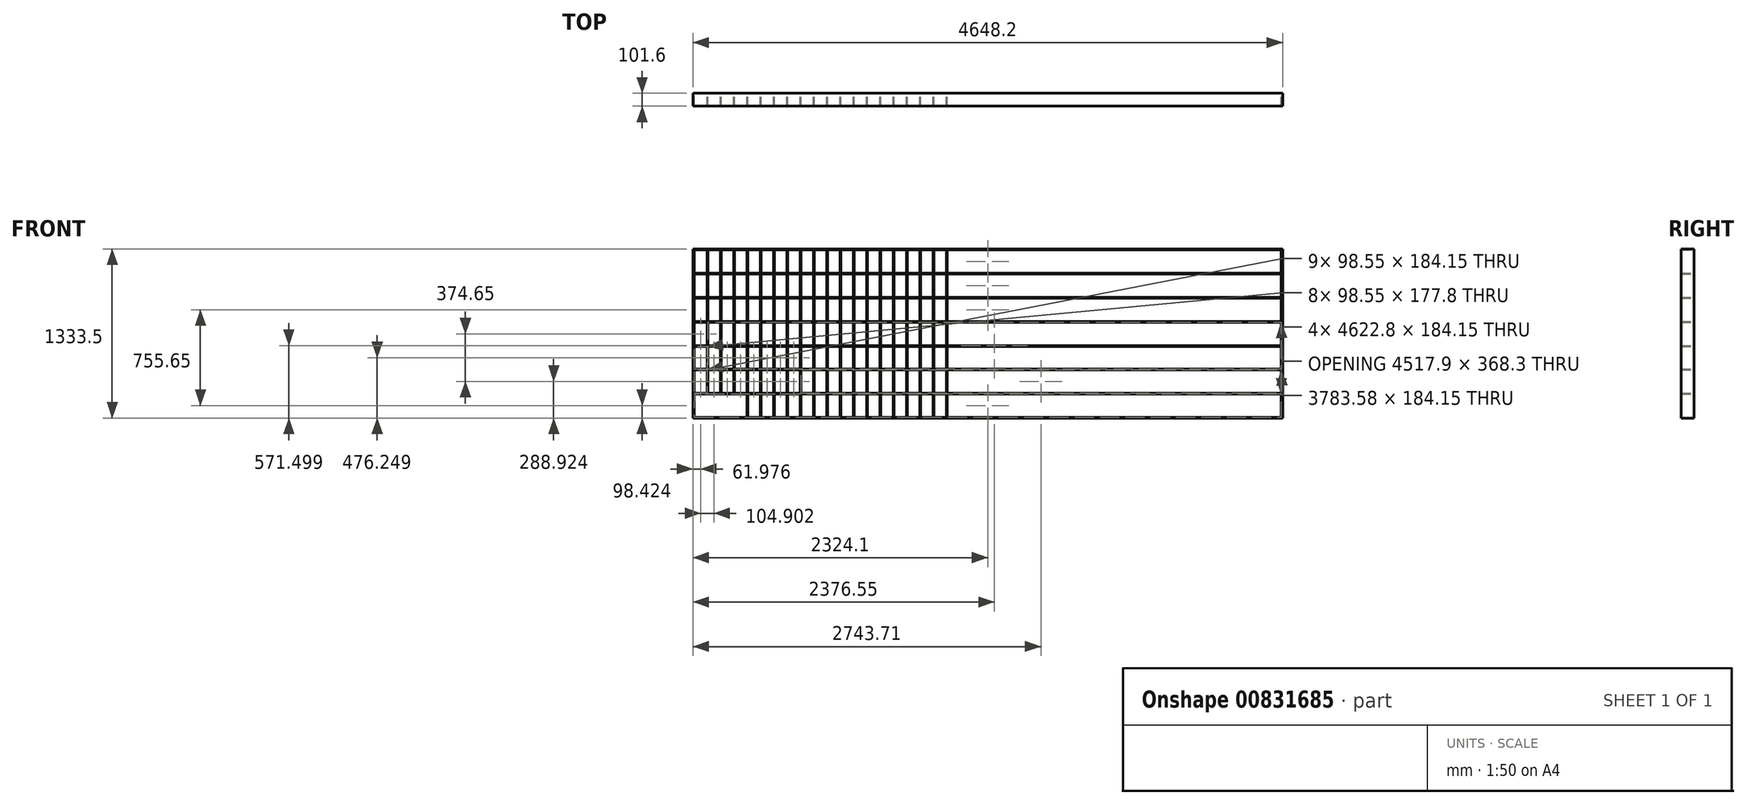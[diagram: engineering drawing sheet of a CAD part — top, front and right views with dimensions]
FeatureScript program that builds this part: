
annotation { "Feature Type Name" : "Feature", "Feature Type Description" : "" }
export const myFeature = defineFeature(function(context is Context, id is Id, definition is map)
    precondition{}
    {
        {
            var Q0;
            Q0=qCreatedBy(makeId("Front.planeOp"),FACE);
            var sketch = newSketch(context, id + "F0", { "sketchPlane" : qUnion([Q0])});
            skLineSegment(sketch, "E0.bottom", {"start": v(-168.1, 48.52) * mm, "end": v(168.1, 48.52) * mm});
            skLineSegment(sketch, "E0.top", {"start": v(-168.1, -48.52) * mm, "end": v(168.1, -48.52) * mm});
            skLineSegment(sketch, "E0.left", {"start": v(-168.1, 48.52) * mm, "end": v(-168.1, -48.52) * mm});
            skLineSegment(sketch, "E0.right", {"start": v(168.1, 48.52) * mm, "end": v(168.1, -48.52) * mm});
            skPoint(sketch, "E0.middle", {"position": v(0, 0) * mm});
            skLineSegment(sketch, "E1.bottom", {"start": v(-2132.34, -583.08) * mm, "end": v(2490.46, -583.08) * mm});
            skLineSegment(sketch, "E1.top", {"start": v(-2132.34, -589.43) * mm, "end": v(2490.46, -589.43) * mm});
            skLineSegment(sketch, "E1.left", {"start": v(-2132.34, -583.08) * mm, "end": v(-2132.34, -589.43) * mm});
            skLineSegment(sketch, "E1.right", {"start": v(2490.46, -583.08) * mm, "end": v(2490.46, -589.43) * mm});
            skLineSegment(sketch, "E2.bottom", {"start": v(-2132.34, -392.58) * mm, "end": v(2490.46, -392.58) * mm});
            skLineSegment(sketch, "E2.top", {"start": v(-2132.34, -398.93) * mm, "end": v(2490.46, -398.93) * mm});
            skLineSegment(sketch, "E2.left", {"start": v(-2132.34, -392.58) * mm, "end": v(-2132.34, -398.93) * mm});
            skLineSegment(sketch, "E2.right", {"start": v(2490.46, -392.58) * mm, "end": v(2490.46, -398.93) * mm});
            skLineSegment(sketch, "E3.bottom", {"start": v(-2132.34, -202.08) * mm, "end": v(2490.46, -202.08) * mm});
            skLineSegment(sketch, "E3.top", {"start": v(-2132.34, -208.43) * mm, "end": v(2490.46, -208.43) * mm});
            skLineSegment(sketch, "E3.left", {"start": v(-2132.34, -202.08) * mm, "end": v(-2132.34, -208.43) * mm});
            skLineSegment(sketch, "E3.right", {"start": v(2490.46, -202.08) * mm, "end": v(2490.46, -208.43) * mm});
            skLineSegment(sketch, "E4.bottom", {"start": v(-2132.34, -17.93) * mm, "end": v(2490.46, -17.93) * mm});
            skLineSegment(sketch, "E4.top", {"start": v(-2132.34, -24.28) * mm, "end": v(2490.46, -24.28) * mm});
            skLineSegment(sketch, "E4.left", {"start": v(-2132.34, -17.93) * mm, "end": v(-2132.34, -24.28) * mm});
            skLineSegment(sketch, "E4.right", {"start": v(2490.46, -17.93) * mm, "end": v(2490.46, -24.28) * mm});
            skLineSegment(sketch, "E5.bottom", {"start": v(-2132.34, 172.57) * mm, "end": v(2490.46, 172.57) * mm});
            skLineSegment(sketch, "E5.top", {"start": v(-2132.34, 166.22) * mm, "end": v(2490.46, 166.22) * mm});
            skLineSegment(sketch, "E5.left", {"start": v(-2132.34, 172.57) * mm, "end": v(-2132.34, 166.22) * mm});
            skLineSegment(sketch, "E5.right", {"start": v(2490.46, 172.57) * mm, "end": v(2490.46, 166.22) * mm});
            skLineSegment(sketch, "E6.bottom", {"start": v(-2132.34, 363.07) * mm, "end": v(2490.46, 363.07) * mm});
            skLineSegment(sketch, "E6.top", {"start": v(-2132.34, 356.72) * mm, "end": v(2490.46, 356.72) * mm});
            skLineSegment(sketch, "E6.left", {"start": v(-2132.34, 363.07) * mm, "end": v(-2132.34, 356.72) * mm});
            skLineSegment(sketch, "E6.right", {"start": v(2490.46, 363.07) * mm, "end": v(2490.46, 356.72) * mm});
            skLineSegment(sketch, "E7.bottom", {"start": v(-2132.34, 553.57) * mm, "end": v(2490.46, 553.57) * mm});
            skLineSegment(sketch, "E7.top", {"start": v(-2132.34, 547.22) * mm, "end": v(2490.46, 547.22) * mm});
            skLineSegment(sketch, "E7.left", {"start": v(-2132.34, 553.57) * mm, "end": v(-2132.34, 547.22) * mm});
            skLineSegment(sketch, "E7.right", {"start": v(2490.46, 553.57) * mm, "end": v(2490.46, 547.22) * mm});
            skLineSegment(sketch, "E8.bottom", {"start": v(-2132.34, 744.07) * mm, "end": v(2490.46, 744.07) * mm});
            skLineSegment(sketch, "E8.top", {"start": v(-2132.34, 737.72) * mm, "end": v(2490.46, 737.72) * mm});
            skLineSegment(sketch, "E8.left", {"start": v(-2132.34, 744.07) * mm, "end": v(-2132.34, 737.72) * mm});
            skLineSegment(sketch, "E8.right", {"start": v(2490.46, 744.07) * mm, "end": v(2490.46, 737.72) * mm});
            skLineSegment(sketch, "E9.bottom", {"start": v(-2132.34, -589.43) * mm, "end": v(-2145.04, -589.43) * mm});
            skLineSegment(sketch, "E9.top", {"start": v(-2132.34, 744.07) * mm, "end": v(-2145.04, 744.07) * mm});
            skLineSegment(sketch, "E9.left", {"start": v(-2132.34, -589.43) * mm, "end": v(-2132.34, 744.07) * mm});
            skLineSegment(sketch, "E9.right", {"start": v(-2145.04, -589.43) * mm, "end": v(-2145.04, 744.07) * mm});
            skLineSegment(sketch, "E10.bottom", {"start": v(2490.46, -589.43) * mm, "end": v(2503.16, -589.43) * mm});
            skLineSegment(sketch, "E10.top", {"start": v(2490.46, 744.07) * mm, "end": v(2503.16, 744.07) * mm});
            skLineSegment(sketch, "E10.left", {"start": v(2490.46, -589.43) * mm, "end": v(2490.46, 744.07) * mm});
            skLineSegment(sketch, "E10.right", {"start": v(2503.16, -589.43) * mm, "end": v(2503.16, 744.07) * mm});
            skLineSegment(sketch, "E11.bottom", {"start": v(-2033.79, -589.43) * mm, "end": v(-2027.44, -589.43) * mm});
            skLineSegment(sketch, "E11.top", {"start": v(-2033.79, 744.07) * mm, "end": v(-2027.44, 744.07) * mm});
            skLineSegment(sketch, "E11.left", {"start": v(-2033.79, -589.43) * mm, "end": v(-2033.79, 744.07) * mm});
            skLineSegment(sketch, "E11.right", {"start": v(-2027.44, -589.43) * mm, "end": v(-2027.44, 744.07) * mm});
            skLineSegment(sketch, "E12.bottom", {"start": v(-1928.89, 744.07) * mm, "end": v(-1922.54, 744.07) * mm});
            skLineSegment(sketch, "E12.top", {"start": v(-1928.89, -589.43) * mm, "end": v(-1922.54, -589.43) * mm});
            skLineSegment(sketch, "E12.left", {"start": v(-1928.89, 744.07) * mm, "end": v(-1928.89, -589.43) * mm});
            skLineSegment(sketch, "E12.right", {"start": v(-1922.54, 744.07) * mm, "end": v(-1922.54, -589.43) * mm});
            skLineSegment(sketch, "E13.bottom", {"start": v(-1823.98, 744.07) * mm, "end": v(-1817.63, 744.07) * mm});
            skLineSegment(sketch, "E13.top", {"start": v(-1823.98, -589.43) * mm, "end": v(-1817.63, -589.43) * mm});
            skLineSegment(sketch, "E13.left", {"start": v(-1823.98, 744.07) * mm, "end": v(-1823.98, -589.43) * mm});
            skLineSegment(sketch, "E13.right", {"start": v(-1817.63, 744.07) * mm, "end": v(-1817.63, -589.43) * mm});
            skLineSegment(sketch, "E14.bottom", {"start": v(-1719.08, 744.07) * mm, "end": v(-1712.73, 744.07) * mm});
            skLineSegment(sketch, "E14.top", {"start": v(-1719.08, -589.43) * mm, "end": v(-1712.73, -589.43) * mm});
            skLineSegment(sketch, "E14.left", {"start": v(-1719.08, 744.07) * mm, "end": v(-1719.08, -589.43) * mm});
            skLineSegment(sketch, "E14.right", {"start": v(-1712.73, 744.07) * mm, "end": v(-1712.73, -589.43) * mm});
            skLineSegment(sketch, "E15.bottom", {"start": v(-1614.18, 744.07) * mm, "end": v(-1607.83, 744.07) * mm});
            skLineSegment(sketch, "E15.top", {"start": v(-1614.18, -589.43) * mm, "end": v(-1607.83, -589.43) * mm});
            skLineSegment(sketch, "E15.left", {"start": v(-1614.18, 744.07) * mm, "end": v(-1614.18, -589.43) * mm});
            skLineSegment(sketch, "E15.right", {"start": v(-1607.83, 744.07) * mm, "end": v(-1607.83, -589.43) * mm});
            skLineSegment(sketch, "E16.bottom", {"start": v(-1509.28, 744.07) * mm, "end": v(-1502.93, 744.07) * mm});
            skLineSegment(sketch, "E16.top", {"start": v(-1509.28, -589.43) * mm, "end": v(-1502.93, -589.43) * mm});
            skLineSegment(sketch, "E16.left", {"start": v(-1509.28, 744.07) * mm, "end": v(-1509.28, -589.43) * mm});
            skLineSegment(sketch, "E16.right", {"start": v(-1502.93, 744.07) * mm, "end": v(-1502.93, -589.43) * mm});
            skLineSegment(sketch, "E17.bottom", {"start": v(-1404.38, 744.07) * mm, "end": v(-1398.03, 744.07) * mm});
            skLineSegment(sketch, "E17.top", {"start": v(-1404.38, -589.43) * mm, "end": v(-1398.03, -589.43) * mm});
            skLineSegment(sketch, "E17.left", {"start": v(-1404.38, 744.07) * mm, "end": v(-1404.38, -589.43) * mm});
            skLineSegment(sketch, "E17.right", {"start": v(-1398.03, 744.07) * mm, "end": v(-1398.03, -589.43) * mm});
            skLineSegment(sketch, "E18.bottom", {"start": v(-1299.47, 744.07) * mm, "end": v(-1293.12, 744.07) * mm});
            skLineSegment(sketch, "E18.top", {"start": v(-1299.47, -589.43) * mm, "end": v(-1293.12, -589.43) * mm});
            skLineSegment(sketch, "E18.left", {"start": v(-1299.47, 744.07) * mm, "end": v(-1299.47, -589.43) * mm});
            skLineSegment(sketch, "E18.right", {"start": v(-1293.12, 744.07) * mm, "end": v(-1293.12, -589.43) * mm});
            skLineSegment(sketch, "E19.bottom", {"start": v(-1194.57, 744.07) * mm, "end": v(-1188.22, 744.07) * mm});
            skLineSegment(sketch, "E19.top", {"start": v(-1194.57, -589.43) * mm, "end": v(-1188.22, -589.43) * mm});
            skLineSegment(sketch, "E19.left", {"start": v(-1194.57, 744.07) * mm, "end": v(-1194.57, -589.43) * mm});
            skLineSegment(sketch, "E19.right", {"start": v(-1188.22, 744.07) * mm, "end": v(-1188.22, -589.43) * mm});
            skLineSegment(sketch, "E20.bottom", {"start": v(-1083.32, 744.07) * mm, "end": v(-1089.67, 744.07) * mm});
            skLineSegment(sketch, "E20.top", {"start": v(-1083.32, -589.43) * mm, "end": v(-1089.67, -589.43) * mm});
            skLineSegment(sketch, "E20.left", {"start": v(-1083.32, 744.07) * mm, "end": v(-1083.32, -589.43) * mm});
            skLineSegment(sketch, "E20.right", {"start": v(-1089.67, 744.07) * mm, "end": v(-1089.67, -589.43) * mm});
            skLineSegment(sketch, "E21.bottom", {"start": v(-984.77, 744.07) * mm, "end": v(-978.42, 744.07) * mm});
            skLineSegment(sketch, "E21.top", {"start": v(-984.77, -589.43) * mm, "end": v(-978.42, -589.43) * mm});
            skLineSegment(sketch, "E21.left", {"start": v(-984.77, 744.07) * mm, "end": v(-984.77, -589.43) * mm});
            skLineSegment(sketch, "E21.right", {"start": v(-978.42, 744.07) * mm, "end": v(-978.42, -589.43) * mm});
            skLineSegment(sketch, "E22.bottom", {"start": v(-879.87, 744.07) * mm, "end": v(-873.52, 744.07) * mm});
            skLineSegment(sketch, "E22.top", {"start": v(-879.87, -589.43) * mm, "end": v(-873.52, -589.43) * mm});
            skLineSegment(sketch, "E22.left", {"start": v(-879.87, 744.07) * mm, "end": v(-879.87, -589.43) * mm});
            skLineSegment(sketch, "E22.right", {"start": v(-873.52, 744.07) * mm, "end": v(-873.52, -589.43) * mm});
            skLineSegment(sketch, "E23.bottom", {"start": v(-774.96, 744.07) * mm, "end": v(-768.61, 744.07) * mm});
            skLineSegment(sketch, "E23.top", {"start": v(-774.96, -589.43) * mm, "end": v(-768.61, -589.43) * mm});
            skLineSegment(sketch, "E23.left", {"start": v(-774.96, 744.07) * mm, "end": v(-774.96, -589.43) * mm});
            skLineSegment(sketch, "E23.right", {"start": v(-768.61, 744.07) * mm, "end": v(-768.61, -589.43) * mm});
            skLineSegment(sketch, "E24.top", {"start": v(-755.75, -589.43) * mm, "end": v(-735.44, -589.43) * mm});
            skLineSegment(sketch, "E25.bottom", {"start": v(-670.06, 744.07) * mm, "end": v(-663.71, 744.07) * mm});
            skLineSegment(sketch, "E25.top", {"start": v(-670.06, -589.43) * mm, "end": v(-663.71, -589.43) * mm});
            skLineSegment(sketch, "E25.left", {"start": v(-670.06, 744.07) * mm, "end": v(-670.06, -589.43) * mm});
            skLineSegment(sketch, "E25.right", {"start": v(-663.71, 744.07) * mm, "end": v(-663.71, -589.43) * mm});
            skLineSegment(sketch, "E26.bottom", {"start": v(-565.16, 744.07) * mm, "end": v(-558.8, 744.07) * mm});
            skLineSegment(sketch, "E26.top", {"start": v(-565.16, -589.43) * mm, "end": v(-558.8, -589.43) * mm});
            skLineSegment(sketch, "E26.left", {"start": v(-565.16, 744.07) * mm, "end": v(-565.16, -589.43) * mm});
            skLineSegment(sketch, "E26.right", {"start": v(-558.8, 744.07) * mm, "end": v(-558.8, -589.43) * mm});
            skLineSegment(sketch, "E27.bottom", {"start": v(-460.26, 744.07) * mm, "end": v(-453.9, 744.07) * mm});
            skLineSegment(sketch, "E27.top", {"start": v(-460.26, -589.43) * mm, "end": v(-453.9, -589.43) * mm});
            skLineSegment(sketch, "E27.left", {"start": v(-460.26, 744.07) * mm, "end": v(-460.26, -589.43) * mm});
            skLineSegment(sketch, "E27.right", {"start": v(-453.9, 744.07) * mm, "end": v(-453.9, -589.43) * mm});
            skLineSegment(sketch, "E28.bottom", {"start": v(-355.36, 744.07) * mm, "end": v(-349, 744.07) * mm});
            skLineSegment(sketch, "E28.top", {"start": v(-355.36, -589.43) * mm, "end": v(-349, -589.43) * mm});
            skLineSegment(sketch, "E28.left", {"start": v(-355.36, 744.07) * mm, "end": v(-355.36, -589.43) * mm});
            skLineSegment(sketch, "E28.right", {"start": v(-349, 744.07) * mm, "end": v(-349, -589.43) * mm});
            skLineSegment(sketch, "E29.bottom", {"start": v(-244.1, 744.07) * mm, "end": v(-250.45, 744.07) * mm});
            skLineSegment(sketch, "E29.top", {"start": v(-244.1, -589.43) * mm, "end": v(-250.45, -589.43) * mm});
            skLineSegment(sketch, "E29.left", {"start": v(-244.1, 744.07) * mm, "end": v(-244.1, -589.43) * mm});
            skLineSegment(sketch, "E29.right", {"start": v(-250.45, 744.07) * mm, "end": v(-250.45, -589.43) * mm});
            skLineSegment(sketch, "E30.bottom", {"start": v(-139.2, 744.07) * mm, "end": v(-145.55, 744.07) * mm});
            skLineSegment(sketch, "E30.top", {"start": v(-139.2, -589.43) * mm, "end": v(-145.55, -589.43) * mm});
            skLineSegment(sketch, "E30.left", {"start": v(-139.2, 744.07) * mm, "end": v(-139.2, -589.43) * mm});
            skLineSegment(sketch, "E30.right", {"start": v(-145.55, 744.07) * mm, "end": v(-145.55, -589.43) * mm});
            skSolve(sketch);
        }
        {
            var Q0;
            {var subQ0=sQuery(id+"F0.wireOp",EDGE,"E1.bottom");Q0=makeQuery(id+"F0.imprint","IMPRINT",FACE,{"disambiguationData":[TD([[makeQuery(id+"F0.imprint","IMPRINT",EDGE,{"derivedFrom":subQ0}),1.0]])]});}
            var sketch = newSketch(context, id + "F1", { "sketchPlane" : qUnion([Q0])});
            skSolve(sketch);
        }
        {
            var Q0;
            Q0 = qSketchRegion(id + "F0", true);
            var Q1;
            {var subQ0=sQuery(id+"F0.wireOp",EDGE,"E7.bottom");Q1=makeQuery(id+"F0.imprint","IMPRINT",FACE,{"disambiguationData":[TD([[makeQuery(id+"F0.imprint","IMPRINT",EDGE,{"derivedFrom":subQ0}),-1.0]])]});}
            var Q2;
            {var subQ0=sQuery(id+"F0.wireOp",EDGE,"E6.bottom");Q2=makeQuery(id+"F0.imprint","IMPRINT",FACE,{"disambiguationData":[TD([[makeQuery(id+"F0.imprint","IMPRINT",EDGE,{"derivedFrom":subQ0}),-1.0]])]});}
            var Q3;
            {var subQ0=sQuery(id+"F0.wireOp",EDGE,"E5.bottom");Q3=makeQuery(id+"F0.imprint","IMPRINT",FACE,{"disambiguationData":[TD([[makeQuery(id+"F0.imprint","IMPRINT",EDGE,{"derivedFrom":subQ0}),-1.0]])]});}
            var Q4;
            {var subQ0=sQuery(id+"F0.wireOp",EDGE,"E4.bottom");var subQ1=sQuery(id+"F0.wireOp",EDGE,"E0.left");var subQ2=makeQuery(id+"F0.imprint","INTERSECT",VERTEX,{"derivedFrom":[subQ1,subQ0]});Q4=makeQuery(id+"F0.imprint","IMPRINT",FACE,{"disambiguationData":[TD([[makeQuery(id+"F0.imprint","IMPRINT",EDGE,{"disambiguationData":[TD([[subQ2,-1.0]])],"derivedFrom":subQ1}),-1.0]])]});}
            var Q5;
            {var subQ0=sQuery(id+"F0.wireOp",EDGE,"E3.bottom");Q5=makeQuery(id+"F0.imprint","IMPRINT",FACE,{"disambiguationData":[TD([[makeQuery(id+"F0.imprint","IMPRINT",EDGE,{"derivedFrom":subQ0}),-1.0]])]});}
            var Q6;
            {var subQ0=sQuery(id+"F0.wireOp",EDGE,"E2.bottom");Q6=makeQuery(id+"F0.imprint","IMPRINT",FACE,{"disambiguationData":[TD([[makeQuery(id+"F0.imprint","IMPRINT",EDGE,{"derivedFrom":subQ0}),-1.0]])]});}
            var Q7;
            {var subQ0=sQuery(id+"F0.wireOp",EDGE,"E4.bottom");var subQ1=sQuery(id+"F0.wireOp",EDGE,"E0.left");var subQ2=makeQuery(id+"F0.imprint","INTERSECT",VERTEX,{"derivedFrom":[subQ1,subQ0]});Q7=makeQuery(id+"F0.imprint","IMPRINT",FACE,{"disambiguationData":[TD([[makeQuery(id+"F0.imprint","IMPRINT",EDGE,{"disambiguationData":[TD([[subQ2,-1.0]])],"derivedFrom":subQ1}),1.0]])]});}
            var Q8;
            {var subQ0=sQuery(id+"F0.wireOp",EDGE,"E4.bottom");var subQ1=sQuery(id+"F0.wireOp",EDGE,"E0.right");var subQ2=makeQuery(id+"F0.imprint","INTERSECT",VERTEX,{"derivedFrom":[subQ1,subQ0]});Q8=makeQuery(id+"F0.imprint","IMPRINT",FACE,{"disambiguationData":[TD([[makeQuery(id+"F0.imprint","IMPRINT",EDGE,{"disambiguationData":[TD([[subQ2,-1.0]])],"derivedFrom":subQ1}),1.0]])]});}
            extrude(context, id + "F2", {"entities" : qUnion([Q0, Q1, Q2, Q3, Q4, Q5, Q6, Q7, Q8]), "depth" : 101.6 * mm, "offsetDistance" : 25.4 * mm});
        }
        {
            var Q0;
            {var subQ0=sQuery(id+"F0.wireOp",EDGE,"E4.bottom");var subQ1=sQuery(id+"F0.wireOp",EDGE,"E0.right");var subQ2=makeQuery(id+"F0.imprint","INTERSECT",VERTEX,{"derivedFrom":[subQ1,subQ0]});Q0=makeQuery(id+"F0.imprint","IMPRINT",FACE,{"disambiguationData":[TD([[makeQuery(id+"F0.imprint","IMPRINT",EDGE,{"disambiguationData":[TD([[subQ2,-1.0]])],"derivedFrom":subQ1}),-1.0]])]});}
            var Q1;
            {var subQ0=sQuery(id+"F0.wireOp",EDGE,"E28.right");var subQ1=sQuery(id+"F0.wireOp",EDGE,"E4.bottom");var subQ2=makeQuery(id+"F0.imprint","INTERSECT",VERTEX,{"derivedFrom":[subQ1,subQ0]});Q1=makeQuery(id+"F0.imprint","IMPRINT",FACE,{"disambiguationData":[TD([[makeQuery(id+"F0.imprint","IMPRINT",EDGE,{"disambiguationData":[TD([[subQ2,-1.0]])],"derivedFrom":subQ1}),-1.0]])]});}
            var Q2;
            {var subQ0=sQuery(id+"F0.wireOp",EDGE,"E27.right");var subQ1=sQuery(id+"F0.wireOp",EDGE,"E4.bottom");var subQ2=makeQuery(id+"F0.imprint","INTERSECT",VERTEX,{"derivedFrom":[subQ1,subQ0]});Q2=makeQuery(id+"F0.imprint","IMPRINT",FACE,{"disambiguationData":[TD([[makeQuery(id+"F0.imprint","IMPRINT",EDGE,{"disambiguationData":[TD([[subQ2,-1.0]])],"derivedFrom":subQ1}),-1.0]])]});}
            var Q3;
            {var subQ0=sQuery(id+"F0.wireOp",EDGE,"E26.right");var subQ1=sQuery(id+"F0.wireOp",EDGE,"E4.bottom");var subQ2=makeQuery(id+"F0.imprint","INTERSECT",VERTEX,{"derivedFrom":[subQ1,subQ0]});Q3=makeQuery(id+"F0.imprint","IMPRINT",FACE,{"disambiguationData":[TD([[makeQuery(id+"F0.imprint","IMPRINT",EDGE,{"disambiguationData":[TD([[subQ2,-1.0]])],"derivedFrom":subQ1}),-1.0]])]});}
            var Q4;
            {var subQ0=sQuery(id+"F0.wireOp",EDGE,"E25.right");var subQ1=sQuery(id+"F0.wireOp",EDGE,"E4.bottom");var subQ2=makeQuery(id+"F0.imprint","INTERSECT",VERTEX,{"derivedFrom":[subQ1,subQ0]});Q4=makeQuery(id+"F0.imprint","IMPRINT",FACE,{"disambiguationData":[TD([[makeQuery(id+"F0.imprint","IMPRINT",EDGE,{"disambiguationData":[TD([[subQ2,-1.0]])],"derivedFrom":subQ1}),-1.0]])]});}
            var Q5;
            {var subQ0=sQuery(id+"F0.wireOp",EDGE,"E23.right");var subQ1=sQuery(id+"F0.wireOp",EDGE,"E4.bottom");var subQ2=makeQuery(id+"F0.imprint","INTERSECT",VERTEX,{"derivedFrom":[subQ1,subQ0]});Q5=makeQuery(id+"F0.imprint","IMPRINT",FACE,{"disambiguationData":[TD([[makeQuery(id+"F0.imprint","IMPRINT",EDGE,{"disambiguationData":[TD([[subQ2,-1.0]])],"derivedFrom":subQ1}),-1.0]])]});}
            var Q6;
            {var subQ0=sQuery(id+"F0.wireOp",EDGE,"E22.right");var subQ1=sQuery(id+"F0.wireOp",EDGE,"E4.bottom");var subQ2=makeQuery(id+"F0.imprint","INTERSECT",VERTEX,{"derivedFrom":[subQ1,subQ0]});Q6=makeQuery(id+"F0.imprint","IMPRINT",FACE,{"disambiguationData":[TD([[makeQuery(id+"F0.imprint","IMPRINT",EDGE,{"disambiguationData":[TD([[subQ2,-1.0]])],"derivedFrom":subQ1}),-1.0]])]});}
            var Q7;
            {var subQ0=sQuery(id+"F0.wireOp",EDGE,"E21.right");var subQ1=sQuery(id+"F0.wireOp",EDGE,"E4.bottom");var subQ2=makeQuery(id+"F0.imprint","INTERSECT",VERTEX,{"derivedFrom":[subQ1,subQ0]});Q7=makeQuery(id+"F0.imprint","IMPRINT",FACE,{"disambiguationData":[TD([[makeQuery(id+"F0.imprint","IMPRINT",EDGE,{"disambiguationData":[TD([[subQ2,-1.0]])],"derivedFrom":subQ1}),-1.0]])]});}
            var Q8;
            {var subQ0=sQuery(id+"F0.wireOp",EDGE,"E19.right");var subQ1=sQuery(id+"F0.wireOp",EDGE,"E4.bottom");var subQ2=makeQuery(id+"F0.imprint","INTERSECT",VERTEX,{"derivedFrom":[subQ1,subQ0]});Q8=makeQuery(id+"F0.imprint","IMPRINT",FACE,{"disambiguationData":[TD([[makeQuery(id+"F0.imprint","IMPRINT",EDGE,{"disambiguationData":[TD([[subQ2,-1.0]])],"derivedFrom":subQ1}),-1.0]])]});}
            var Q9;
            {var subQ0=sQuery(id+"F0.wireOp",EDGE,"E20.left");var subQ1=sQuery(id+"F0.wireOp",EDGE,"E4.bottom");var subQ2=makeQuery(id+"F0.imprint","INTERSECT",VERTEX,{"derivedFrom":[subQ1,subQ0]});Q9=makeQuery(id+"F0.imprint","IMPRINT",FACE,{"disambiguationData":[TD([[makeQuery(id+"F0.imprint","IMPRINT",EDGE,{"disambiguationData":[TD([[subQ2,-1.0]])],"derivedFrom":subQ1}),-1.0]])]});}
            var Q10;
            {var subQ0=sQuery(id+"F0.wireOp",EDGE,"E9.left");var subQ1=sQuery(id+"F0.wireOp",EDGE,"E4.bottom");var subQ2=makeQuery(id+"F0.imprint","INTERSECT",VERTEX,{"derivedFrom":[subQ1,subQ0]});Q10=makeQuery(id+"F0.imprint","IMPRINT",FACE,{"disambiguationData":[TD([[makeQuery(id+"F0.imprint","IMPRINT",EDGE,{"disambiguationData":[TD([[subQ2,-1.0]])],"derivedFrom":subQ1}),-1.0]])]});}
            var Q11;
            {var subQ0=sQuery(id+"F0.wireOp",EDGE,"E11.left");var subQ1=sQuery(id+"F0.wireOp",EDGE,"E1.bottom");var subQ2=makeQuery(id+"F0.imprint","INTERSECT",VERTEX,{"derivedFrom":[subQ1,subQ0]});Q11=makeQuery(id+"F1.imprint","IMPRINT",FACE,{"disambiguationData":[TD([[makeQuery(id+"F1.imprint","IMPRINT",EDGE,{"derivedFrom":makeQuery(id+"F0.imprint","IMPRINT",EDGE,{"disambiguationData":[TD([[subQ2,-1.0]])],"derivedFrom":subQ1})}),1.0]])]});}
            var Q12;
            {var subQ0=sQuery(id+"F0.wireOp",EDGE,"E11.left");var subQ1=sQuery(id+"F0.wireOp",EDGE,"E2.bottom");var subQ2=makeQuery(id+"F0.imprint","INTERSECT",VERTEX,{"derivedFrom":[subQ1,subQ0]});Q12=makeQuery(id+"F0.imprint","IMPRINT",FACE,{"disambiguationData":[TD([[makeQuery(id+"F0.imprint","IMPRINT",EDGE,{"disambiguationData":[TD([[subQ2,-1.0]])],"derivedFrom":subQ1}),1.0]])]});}
            var Q13;
            {var subQ0=sQuery(id+"F0.wireOp",EDGE,"E11.left");var subQ1=sQuery(id+"F0.wireOp",EDGE,"E3.bottom");var subQ2=makeQuery(id+"F0.imprint","INTERSECT",VERTEX,{"derivedFrom":[subQ1,subQ0]});Q13=makeQuery(id+"F0.imprint","IMPRINT",FACE,{"disambiguationData":[TD([[makeQuery(id+"F0.imprint","IMPRINT",EDGE,{"disambiguationData":[TD([[subQ2,-1.0]])],"derivedFrom":subQ1}),1.0]])]});}
            var Q14;
            {var subQ0=sQuery(id+"F0.wireOp",EDGE,"E11.right");var subQ1=sQuery(id+"F0.wireOp",EDGE,"E4.bottom");var subQ2=makeQuery(id+"F0.imprint","INTERSECT",VERTEX,{"derivedFrom":[subQ1,subQ0]});Q14=makeQuery(id+"F0.imprint","IMPRINT",FACE,{"disambiguationData":[TD([[makeQuery(id+"F0.imprint","IMPRINT",EDGE,{"disambiguationData":[TD([[subQ2,-1.0]])],"derivedFrom":subQ1}),-1.0]])]});}
            var Q15;
            {var subQ0=sQuery(id+"F0.wireOp",EDGE,"E18.right");var subQ1=sQuery(id+"F0.wireOp",EDGE,"E4.bottom");var subQ2=makeQuery(id+"F0.imprint","INTERSECT",VERTEX,{"derivedFrom":[subQ1,subQ0]});Q15=makeQuery(id+"F0.imprint","IMPRINT",FACE,{"disambiguationData":[TD([[makeQuery(id+"F0.imprint","IMPRINT",EDGE,{"disambiguationData":[TD([[subQ2,-1.0]])],"derivedFrom":subQ1}),-1.0]])]});}
            var Q16;
            {var subQ0=sQuery(id+"F0.wireOp",EDGE,"E17.right");var subQ1=sQuery(id+"F0.wireOp",EDGE,"E4.bottom");var subQ2=makeQuery(id+"F0.imprint","INTERSECT",VERTEX,{"derivedFrom":[subQ1,subQ0]});Q16=makeQuery(id+"F0.imprint","IMPRINT",FACE,{"disambiguationData":[TD([[makeQuery(id+"F0.imprint","IMPRINT",EDGE,{"disambiguationData":[TD([[subQ2,-1.0]])],"derivedFrom":subQ1}),-1.0]])]});}
            var Q17;
            {var subQ0=sQuery(id+"F0.wireOp",EDGE,"E16.right");var subQ1=sQuery(id+"F0.wireOp",EDGE,"E4.bottom");var subQ2=makeQuery(id+"F0.imprint","INTERSECT",VERTEX,{"derivedFrom":[subQ1,subQ0]});Q17=makeQuery(id+"F0.imprint","IMPRINT",FACE,{"disambiguationData":[TD([[makeQuery(id+"F0.imprint","IMPRINT",EDGE,{"disambiguationData":[TD([[subQ2,-1.0]])],"derivedFrom":subQ1}),-1.0]])]});}
            var Q18;
            {var subQ0=sQuery(id+"F0.wireOp",EDGE,"E15.right");var subQ1=sQuery(id+"F0.wireOp",EDGE,"E4.bottom");var subQ2=makeQuery(id+"F0.imprint","INTERSECT",VERTEX,{"derivedFrom":[subQ1,subQ0]});Q18=makeQuery(id+"F0.imprint","IMPRINT",FACE,{"disambiguationData":[TD([[makeQuery(id+"F0.imprint","IMPRINT",EDGE,{"disambiguationData":[TD([[subQ2,-1.0]])],"derivedFrom":subQ1}),-1.0]])]});}
            var Q19;
            {var subQ0=sQuery(id+"F0.wireOp",EDGE,"E14.right");var subQ1=sQuery(id+"F0.wireOp",EDGE,"E4.bottom");var subQ2=makeQuery(id+"F0.imprint","INTERSECT",VERTEX,{"derivedFrom":[subQ1,subQ0]});Q19=makeQuery(id+"F0.imprint","IMPRINT",FACE,{"disambiguationData":[TD([[makeQuery(id+"F0.imprint","IMPRINT",EDGE,{"disambiguationData":[TD([[subQ2,-1.0]])],"derivedFrom":subQ1}),-1.0]])]});}
            var Q20;
            {var subQ0=sQuery(id+"F0.wireOp",EDGE,"E13.right");var subQ1=sQuery(id+"F0.wireOp",EDGE,"E4.bottom");var subQ2=makeQuery(id+"F0.imprint","INTERSECT",VERTEX,{"derivedFrom":[subQ1,subQ0]});Q20=makeQuery(id+"F0.imprint","IMPRINT",FACE,{"disambiguationData":[TD([[makeQuery(id+"F0.imprint","IMPRINT",EDGE,{"disambiguationData":[TD([[subQ2,-1.0]])],"derivedFrom":subQ1}),-1.0]])]});}
            var Q21;
            {var subQ0=sQuery(id+"F0.wireOp",EDGE,"E18.left");var subQ1=sQuery(id+"F0.wireOp",EDGE,"E3.bottom");var subQ2=makeQuery(id+"F0.imprint","INTERSECT",VERTEX,{"derivedFrom":[subQ1,subQ0]});Q21=makeQuery(id+"F0.imprint","IMPRINT",FACE,{"disambiguationData":[TD([[makeQuery(id+"F0.imprint","IMPRINT",EDGE,{"disambiguationData":[TD([[subQ2,-1.0]])],"derivedFrom":subQ1}),1.0]])]});}
            var Q22;
            {var subQ0=sQuery(id+"F0.wireOp",EDGE,"E17.left");var subQ1=sQuery(id+"F0.wireOp",EDGE,"E3.bottom");var subQ2=makeQuery(id+"F0.imprint","INTERSECT",VERTEX,{"derivedFrom":[subQ1,subQ0]});Q22=makeQuery(id+"F0.imprint","IMPRINT",FACE,{"disambiguationData":[TD([[makeQuery(id+"F0.imprint","IMPRINT",EDGE,{"disambiguationData":[TD([[subQ2,-1.0]])],"derivedFrom":subQ1}),1.0]])]});}
            var Q23;
            {var subQ0=sQuery(id+"F0.wireOp",EDGE,"E16.left");var subQ1=sQuery(id+"F0.wireOp",EDGE,"E3.bottom");var subQ2=makeQuery(id+"F0.imprint","INTERSECT",VERTEX,{"derivedFrom":[subQ1,subQ0]});Q23=makeQuery(id+"F0.imprint","IMPRINT",FACE,{"disambiguationData":[TD([[makeQuery(id+"F0.imprint","IMPRINT",EDGE,{"disambiguationData":[TD([[subQ2,-1.0]])],"derivedFrom":subQ1}),1.0]])]});}
            var Q24;
            {var subQ0=sQuery(id+"F0.wireOp",EDGE,"E12.right");var subQ1=sQuery(id+"F0.wireOp",EDGE,"E4.bottom");var subQ2=makeQuery(id+"F0.imprint","INTERSECT",VERTEX,{"derivedFrom":[subQ1,subQ0]});Q24=makeQuery(id+"F0.imprint","IMPRINT",FACE,{"disambiguationData":[TD([[makeQuery(id+"F0.imprint","IMPRINT",EDGE,{"disambiguationData":[TD([[subQ2,-1.0]])],"derivedFrom":subQ1}),-1.0]])]});}
            var Q25;
            {var subQ0=sQuery(id+"F0.wireOp",EDGE,"E12.left");var subQ1=sQuery(id+"F0.wireOp",EDGE,"E3.bottom");var subQ2=makeQuery(id+"F0.imprint","INTERSECT",VERTEX,{"derivedFrom":[subQ1,subQ0]});Q25=makeQuery(id+"F0.imprint","IMPRINT",FACE,{"disambiguationData":[TD([[makeQuery(id+"F0.imprint","IMPRINT",EDGE,{"disambiguationData":[TD([[subQ2,-1.0]])],"derivedFrom":subQ1}),1.0]])]});}
            var Q26;
            {var subQ0=sQuery(id+"F0.wireOp",EDGE,"E13.left");var subQ1=sQuery(id+"F0.wireOp",EDGE,"E3.bottom");var subQ2=makeQuery(id+"F0.imprint","INTERSECT",VERTEX,{"derivedFrom":[subQ1,subQ0]});Q26=makeQuery(id+"F0.imprint","IMPRINT",FACE,{"disambiguationData":[TD([[makeQuery(id+"F0.imprint","IMPRINT",EDGE,{"disambiguationData":[TD([[subQ2,-1.0]])],"derivedFrom":subQ1}),1.0]])]});}
            var Q27;
            {var subQ0=sQuery(id+"F0.wireOp",EDGE,"E14.left");var subQ1=sQuery(id+"F0.wireOp",EDGE,"E3.bottom");var subQ2=makeQuery(id+"F0.imprint","INTERSECT",VERTEX,{"derivedFrom":[subQ1,subQ0]});Q27=makeQuery(id+"F0.imprint","IMPRINT",FACE,{"disambiguationData":[TD([[makeQuery(id+"F0.imprint","IMPRINT",EDGE,{"disambiguationData":[TD([[subQ2,-1.0]])],"derivedFrom":subQ1}),1.0]])]});}
            var Q28;
            {var subQ0=sQuery(id+"F0.wireOp",EDGE,"E15.left");var subQ1=sQuery(id+"F0.wireOp",EDGE,"E3.bottom");var subQ2=makeQuery(id+"F0.imprint","INTERSECT",VERTEX,{"derivedFrom":[subQ1,subQ0]});Q28=makeQuery(id+"F0.imprint","IMPRINT",FACE,{"disambiguationData":[TD([[makeQuery(id+"F0.imprint","IMPRINT",EDGE,{"disambiguationData":[TD([[subQ2,-1.0]])],"derivedFrom":subQ1}),1.0]])]});}
            var Q29;
            {var subQ0=sQuery(id+"F0.wireOp",EDGE,"E15.left");var subQ1=sQuery(id+"F0.wireOp",EDGE,"E2.bottom");var subQ2=makeQuery(id+"F0.imprint","INTERSECT",VERTEX,{"derivedFrom":[subQ1,subQ0]});Q29=makeQuery(id+"F0.imprint","IMPRINT",FACE,{"disambiguationData":[TD([[makeQuery(id+"F0.imprint","IMPRINT",EDGE,{"disambiguationData":[TD([[subQ2,-1.0]])],"derivedFrom":subQ1}),1.0]])]});}
            var Q30;
            {var subQ0=sQuery(id+"F0.wireOp",EDGE,"E16.left");var subQ1=sQuery(id+"F0.wireOp",EDGE,"E2.bottom");var subQ2=makeQuery(id+"F0.imprint","INTERSECT",VERTEX,{"derivedFrom":[subQ1,subQ0]});Q30=makeQuery(id+"F0.imprint","IMPRINT",FACE,{"disambiguationData":[TD([[makeQuery(id+"F0.imprint","IMPRINT",EDGE,{"disambiguationData":[TD([[subQ2,-1.0]])],"derivedFrom":subQ1}),1.0]])]});}
            var Q31;
            {var subQ0=sQuery(id+"F0.wireOp",EDGE,"E17.left");var subQ1=sQuery(id+"F0.wireOp",EDGE,"E2.bottom");var subQ2=makeQuery(id+"F0.imprint","INTERSECT",VERTEX,{"derivedFrom":[subQ1,subQ0]});Q31=makeQuery(id+"F0.imprint","IMPRINT",FACE,{"disambiguationData":[TD([[makeQuery(id+"F0.imprint","IMPRINT",EDGE,{"disambiguationData":[TD([[subQ2,-1.0]])],"derivedFrom":subQ1}),1.0]])]});}
            var Q32;
            {var subQ0=sQuery(id+"F0.wireOp",EDGE,"E18.left");var subQ1=sQuery(id+"F0.wireOp",EDGE,"E2.bottom");var subQ2=makeQuery(id+"F0.imprint","INTERSECT",VERTEX,{"derivedFrom":[subQ1,subQ0]});Q32=makeQuery(id+"F0.imprint","IMPRINT",FACE,{"disambiguationData":[TD([[makeQuery(id+"F0.imprint","IMPRINT",EDGE,{"disambiguationData":[TD([[subQ2,-1.0]])],"derivedFrom":subQ1}),1.0]])]});}
            var Q33;
            {var subQ0=sQuery(id+"F0.wireOp",EDGE,"E18.left");var subQ1=sQuery(id+"F0.wireOp",EDGE,"E4.bottom");var subQ2=makeQuery(id+"F0.imprint","INTERSECT",VERTEX,{"derivedFrom":[subQ1,subQ0]});Q33=makeQuery(id+"F0.imprint","IMPRINT",FACE,{"disambiguationData":[TD([[makeQuery(id+"F0.imprint","IMPRINT",EDGE,{"disambiguationData":[TD([[subQ2,-1.0]])],"derivedFrom":subQ1}),-1.0]])]});}
            var Q34;
            {var subQ0=sQuery(id+"F0.wireOp",EDGE,"E19.left");var subQ1=sQuery(id+"F0.wireOp",EDGE,"E4.bottom");var subQ2=makeQuery(id+"F0.imprint","INTERSECT",VERTEX,{"derivedFrom":[subQ1,subQ0]});Q34=makeQuery(id+"F0.imprint","IMPRINT",FACE,{"disambiguationData":[TD([[makeQuery(id+"F0.imprint","IMPRINT",EDGE,{"disambiguationData":[TD([[subQ2,-1.0]])],"derivedFrom":subQ1}),-1.0]])]});}
            var Q35;
            {var subQ0=sQuery(id+"F0.wireOp",EDGE,"E17.left");var subQ1=sQuery(id+"F0.wireOp",EDGE,"E4.bottom");var subQ2=makeQuery(id+"F0.imprint","INTERSECT",VERTEX,{"derivedFrom":[subQ1,subQ0]});Q35=makeQuery(id+"F0.imprint","IMPRINT",FACE,{"disambiguationData":[TD([[makeQuery(id+"F0.imprint","IMPRINT",EDGE,{"disambiguationData":[TD([[subQ2,-1.0]])],"derivedFrom":subQ1}),-1.0]])]});}
            var Q36;
            {var subQ0=sQuery(id+"F0.wireOp",EDGE,"E16.left");var subQ1=sQuery(id+"F0.wireOp",EDGE,"E4.bottom");var subQ2=makeQuery(id+"F0.imprint","INTERSECT",VERTEX,{"derivedFrom":[subQ1,subQ0]});Q36=makeQuery(id+"F0.imprint","IMPRINT",FACE,{"disambiguationData":[TD([[makeQuery(id+"F0.imprint","IMPRINT",EDGE,{"disambiguationData":[TD([[subQ2,-1.0]])],"derivedFrom":subQ1}),-1.0]])]});}
            var Q37;
            {var subQ0=sQuery(id+"F0.wireOp",EDGE,"E15.left");var subQ1=sQuery(id+"F0.wireOp",EDGE,"E4.bottom");var subQ2=makeQuery(id+"F0.imprint","INTERSECT",VERTEX,{"derivedFrom":[subQ1,subQ0]});Q37=makeQuery(id+"F0.imprint","IMPRINT",FACE,{"disambiguationData":[TD([[makeQuery(id+"F0.imprint","IMPRINT",EDGE,{"disambiguationData":[TD([[subQ2,-1.0]])],"derivedFrom":subQ1}),-1.0]])]});}
            var Q38;
            {var subQ0=sQuery(id+"F0.wireOp",EDGE,"E14.left");var subQ1=sQuery(id+"F0.wireOp",EDGE,"E4.bottom");var subQ2=makeQuery(id+"F0.imprint","INTERSECT",VERTEX,{"derivedFrom":[subQ1,subQ0]});Q38=makeQuery(id+"F0.imprint","IMPRINT",FACE,{"disambiguationData":[TD([[makeQuery(id+"F0.imprint","IMPRINT",EDGE,{"disambiguationData":[TD([[subQ2,-1.0]])],"derivedFrom":subQ1}),-1.0]])]});}
            var Q39;
            {var subQ0=sQuery(id+"F0.wireOp",EDGE,"E13.left");var subQ1=sQuery(id+"F0.wireOp",EDGE,"E4.bottom");var subQ2=makeQuery(id+"F0.imprint","INTERSECT",VERTEX,{"derivedFrom":[subQ1,subQ0]});Q39=makeQuery(id+"F0.imprint","IMPRINT",FACE,{"disambiguationData":[TD([[makeQuery(id+"F0.imprint","IMPRINT",EDGE,{"disambiguationData":[TD([[subQ2,-1.0]])],"derivedFrom":subQ1}),-1.0]])]});}
            var Q40;
            {var subQ0=sQuery(id+"F0.wireOp",EDGE,"E12.left");var subQ1=sQuery(id+"F0.wireOp",EDGE,"E4.bottom");var subQ2=makeQuery(id+"F0.imprint","INTERSECT",VERTEX,{"derivedFrom":[subQ1,subQ0]});Q40=makeQuery(id+"F0.imprint","IMPRINT",FACE,{"disambiguationData":[TD([[makeQuery(id+"F0.imprint","IMPRINT",EDGE,{"disambiguationData":[TD([[subQ2,-1.0]])],"derivedFrom":subQ1}),-1.0]])]});}
            var Q41;
            {var subQ0=sQuery(id+"F0.wireOp",EDGE,"E11.left");var subQ1=sQuery(id+"F0.wireOp",EDGE,"E4.bottom");var subQ2=makeQuery(id+"F0.imprint","INTERSECT",VERTEX,{"derivedFrom":[subQ1,subQ0]});Q41=makeQuery(id+"F0.imprint","IMPRINT",FACE,{"disambiguationData":[TD([[makeQuery(id+"F0.imprint","IMPRINT",EDGE,{"disambiguationData":[TD([[subQ2,-1.0]])],"derivedFrom":subQ1}),-1.0]])]});}
            var Q42;
            {var subQ0=sQuery(id+"F0.wireOp",EDGE,"E11.left");var subQ1=sQuery(id+"F0.wireOp",EDGE,"E4.bottom");var subQ2=makeQuery(id+"F0.imprint","INTERSECT",VERTEX,{"derivedFrom":[subQ1,subQ0]});Q42=makeQuery(id+"F0.imprint","IMPRINT",FACE,{"disambiguationData":[TD([[makeQuery(id+"F0.imprint","IMPRINT",EDGE,{"disambiguationData":[TD([[subQ2,-1.0]])],"derivedFrom":subQ1}),1.0]])]});}
            var Q43;
            {var subQ0=sQuery(id+"F0.wireOp",EDGE,"E12.left");var subQ1=sQuery(id+"F0.wireOp",EDGE,"E2.bottom");var subQ2=makeQuery(id+"F0.imprint","INTERSECT",VERTEX,{"derivedFrom":[subQ1,subQ0]});Q43=makeQuery(id+"F0.imprint","IMPRINT",FACE,{"disambiguationData":[TD([[makeQuery(id+"F0.imprint","IMPRINT",EDGE,{"disambiguationData":[TD([[subQ2,-1.0]])],"derivedFrom":subQ1}),1.0]])]});}
            var Q44;
            {var subQ0=sQuery(id+"F0.wireOp",EDGE,"E13.left");var subQ1=sQuery(id+"F0.wireOp",EDGE,"E2.bottom");var subQ2=makeQuery(id+"F0.imprint","INTERSECT",VERTEX,{"derivedFrom":[subQ1,subQ0]});Q44=makeQuery(id+"F0.imprint","IMPRINT",FACE,{"disambiguationData":[TD([[makeQuery(id+"F0.imprint","IMPRINT",EDGE,{"disambiguationData":[TD([[subQ2,-1.0]])],"derivedFrom":subQ1}),1.0]])]});}
            var Q45;
            {var subQ0=sQuery(id+"F0.wireOp",EDGE,"E14.left");var subQ1=sQuery(id+"F0.wireOp",EDGE,"E2.bottom");var subQ2=makeQuery(id+"F0.imprint","INTERSECT",VERTEX,{"derivedFrom":[subQ1,subQ0]});Q45=makeQuery(id+"F0.imprint","IMPRINT",FACE,{"disambiguationData":[TD([[makeQuery(id+"F0.imprint","IMPRINT",EDGE,{"disambiguationData":[TD([[subQ2,-1.0]])],"derivedFrom":subQ1}),1.0]])]});}
            var Q46;
            {var subQ0=sQuery(id+"F0.wireOp",EDGE,"E12.left");var subQ1=sQuery(id+"F0.wireOp",EDGE,"E1.bottom");var subQ2=makeQuery(id+"F0.imprint","INTERSECT",VERTEX,{"derivedFrom":[subQ1,subQ0]});Q46=makeQuery(id+"F1.imprint","IMPRINT",FACE,{"disambiguationData":[TD([[makeQuery(id+"F1.imprint","IMPRINT",EDGE,{"derivedFrom":makeQuery(id+"F0.imprint","IMPRINT",EDGE,{"disambiguationData":[TD([[subQ2,-1.0]])],"derivedFrom":subQ1})}),1.0]])]});}
            var Q47;
            {var subQ0=sQuery(id+"F0.wireOp",EDGE,"E13.left");var subQ1=sQuery(id+"F0.wireOp",EDGE,"E1.bottom");var subQ2=makeQuery(id+"F0.imprint","INTERSECT",VERTEX,{"derivedFrom":[subQ1,subQ0]});Q47=makeQuery(id+"F1.imprint","IMPRINT",FACE,{"disambiguationData":[TD([[makeQuery(id+"F1.imprint","IMPRINT",EDGE,{"derivedFrom":makeQuery(id+"F0.imprint","IMPRINT",EDGE,{"disambiguationData":[TD([[subQ2,-1.0]])],"derivedFrom":subQ1})}),1.0]])]});}
            extrude(context, id + "F3", {"entities" : qUnion([Q0, Q1, Q2, Q3, Q4, Q5, Q6, Q7, Q8, Q9, Q10, Q11, Q12, Q13, Q14, Q15, Q16, Q17, Q18, Q19, Q20, Q21, Q22, Q23, Q24, Q25, Q26, Q27, Q28, Q29, Q30, Q31, Q32, Q33, Q34, Q35, Q36, Q37, Q38, Q39, Q40, Q41, Q42, Q43, Q44, Q45, Q46, Q47]), "operationType" : NewBodyOperationType.ADD, "depth" : 101.6 * mm, "offsetDistance" : 25.4 * mm});
        }
        {
            var Q0;
            {var subQ0=sQuery(id+"F0.wireOp",EDGE,"E12.left");var subQ1=sQuery(id+"F0.wireOp",EDGE,"E4.bottom");var subQ2=makeQuery(id+"F0.imprint","INTERSECT",VERTEX,{"derivedFrom":[subQ1,subQ0]});Q0=makeQuery(id+"F0.imprint","IMPRINT",FACE,{"disambiguationData":[TD([[makeQuery(id+"F0.imprint","IMPRINT",EDGE,{"disambiguationData":[TD([[subQ2,-1.0]])],"derivedFrom":subQ1}),1.0]])]});}
            var Q1;
            {var subQ0=sQuery(id+"F0.wireOp",EDGE,"E13.left");var subQ1=sQuery(id+"F0.wireOp",EDGE,"E4.bottom");var subQ2=makeQuery(id+"F0.imprint","INTERSECT",VERTEX,{"derivedFrom":[subQ1,subQ0]});Q1=makeQuery(id+"F0.imprint","IMPRINT",FACE,{"disambiguationData":[TD([[makeQuery(id+"F0.imprint","IMPRINT",EDGE,{"disambiguationData":[TD([[subQ2,-1.0]])],"derivedFrom":subQ1}),1.0]])]});}
            var Q2;
            {var subQ0=sQuery(id+"F0.wireOp",EDGE,"E14.left");var subQ1=sQuery(id+"F0.wireOp",EDGE,"E1.bottom");var subQ2=makeQuery(id+"F0.imprint","INTERSECT",VERTEX,{"derivedFrom":[subQ1,subQ0]});Q2=makeQuery(id+"F0.imprint","IMPRINT",FACE,{"disambiguationData":[TD([[makeQuery(id+"F0.imprint","IMPRINT",EDGE,{"disambiguationData":[TD([[subQ2,-1.0]])],"derivedFrom":subQ1}),1.0]])]});}
            var Q3;
            {var subQ0=sQuery(id+"F0.wireOp",EDGE,"E15.left");var subQ1=sQuery(id+"F0.wireOp",EDGE,"E1.bottom");var subQ2=makeQuery(id+"F0.imprint","INTERSECT",VERTEX,{"derivedFrom":[subQ1,subQ0]});Q3=makeQuery(id+"F0.imprint","IMPRINT",FACE,{"disambiguationData":[TD([[makeQuery(id+"F0.imprint","IMPRINT",EDGE,{"disambiguationData":[TD([[subQ2,-1.0]])],"derivedFrom":subQ1}),1.0]])]});}
            var Q4;
            {var subQ0=sQuery(id+"F0.wireOp",EDGE,"E16.left");var subQ1=sQuery(id+"F0.wireOp",EDGE,"E1.bottom");var subQ2=makeQuery(id+"F0.imprint","INTERSECT",VERTEX,{"derivedFrom":[subQ1,subQ0]});Q4=makeQuery(id+"F0.imprint","IMPRINT",FACE,{"disambiguationData":[TD([[makeQuery(id+"F0.imprint","IMPRINT",EDGE,{"disambiguationData":[TD([[subQ2,-1.0]])],"derivedFrom":subQ1}),1.0]])]});}
            var Q5;
            {var subQ0=sQuery(id+"F0.wireOp",EDGE,"E17.left");var subQ1=sQuery(id+"F0.wireOp",EDGE,"E1.bottom");var subQ2=makeQuery(id+"F0.imprint","INTERSECT",VERTEX,{"derivedFrom":[subQ1,subQ0]});Q5=makeQuery(id+"F0.imprint","IMPRINT",FACE,{"disambiguationData":[TD([[makeQuery(id+"F0.imprint","IMPRINT",EDGE,{"disambiguationData":[TD([[subQ2,-1.0]])],"derivedFrom":subQ1}),1.0]])]});}
            var Q6;
            {var subQ0=sQuery(id+"F0.wireOp",EDGE,"E18.left");var subQ1=sQuery(id+"F0.wireOp",EDGE,"E1.bottom");var subQ2=makeQuery(id+"F0.imprint","INTERSECT",VERTEX,{"derivedFrom":[subQ1,subQ0]});Q6=makeQuery(id+"F0.imprint","IMPRINT",FACE,{"disambiguationData":[TD([[makeQuery(id+"F0.imprint","IMPRINT",EDGE,{"disambiguationData":[TD([[subQ2,-1.0]])],"derivedFrom":subQ1}),1.0]])]});}
            var Q7;
            {var subQ0=sQuery(id+"F0.wireOp",EDGE,"E19.left");var subQ1=sQuery(id+"F0.wireOp",EDGE,"E1.bottom");var subQ2=makeQuery(id+"F0.imprint","INTERSECT",VERTEX,{"derivedFrom":[subQ1,subQ0]});Q7=makeQuery(id+"F0.imprint","IMPRINT",FACE,{"disambiguationData":[TD([[makeQuery(id+"F0.imprint","IMPRINT",EDGE,{"disambiguationData":[TD([[subQ2,-1.0]])],"derivedFrom":subQ1}),1.0]])]});}
            var Q8;
            {var subQ0=sQuery(id+"F0.wireOp",EDGE,"E20.right");var subQ1=sQuery(id+"F0.wireOp",EDGE,"E1.bottom");var subQ2=makeQuery(id+"F0.imprint","INTERSECT",VERTEX,{"derivedFrom":[subQ1,subQ0]});Q8=makeQuery(id+"F0.imprint","IMPRINT",FACE,{"disambiguationData":[TD([[makeQuery(id+"F0.imprint","IMPRINT",EDGE,{"disambiguationData":[TD([[subQ2,-1.0]])],"derivedFrom":subQ1}),1.0]])]});}
            var Q9;
            {var subQ0=sQuery(id+"F0.wireOp",EDGE,"E21.left");var subQ1=sQuery(id+"F0.wireOp",EDGE,"E1.bottom");var subQ2=makeQuery(id+"F0.imprint","INTERSECT",VERTEX,{"derivedFrom":[subQ1,subQ0]});Q9=makeQuery(id+"F0.imprint","IMPRINT",FACE,{"disambiguationData":[TD([[makeQuery(id+"F0.imprint","IMPRINT",EDGE,{"disambiguationData":[TD([[subQ2,-1.0]])],"derivedFrom":subQ1}),1.0]])]});}
            var Q10;
            {var subQ0=sQuery(id+"F0.wireOp",EDGE,"E22.left");var subQ1=sQuery(id+"F0.wireOp",EDGE,"E1.bottom");var subQ2=makeQuery(id+"F0.imprint","INTERSECT",VERTEX,{"derivedFrom":[subQ1,subQ0]});Q10=makeQuery(id+"F0.imprint","IMPRINT",FACE,{"disambiguationData":[TD([[makeQuery(id+"F0.imprint","IMPRINT",EDGE,{"disambiguationData":[TD([[subQ2,-1.0]])],"derivedFrom":subQ1}),1.0]])]});}
            var Q11;
            {var subQ0=sQuery(id+"F0.wireOp",EDGE,"E23.left");var subQ1=sQuery(id+"F0.wireOp",EDGE,"E1.bottom");var subQ2=makeQuery(id+"F0.imprint","INTERSECT",VERTEX,{"derivedFrom":[subQ1,subQ0]});Q11=makeQuery(id+"F0.imprint","IMPRINT",FACE,{"disambiguationData":[TD([[makeQuery(id+"F0.imprint","IMPRINT",EDGE,{"disambiguationData":[TD([[subQ2,-1.0]])],"derivedFrom":subQ1}),1.0]])]});}
            var Q12;
            {var subQ0=sQuery(id+"F0.wireOp",EDGE,"E14.left");var subQ1=sQuery(id+"F0.wireOp",EDGE,"E4.bottom");var subQ2=makeQuery(id+"F0.imprint","INTERSECT",VERTEX,{"derivedFrom":[subQ1,subQ0]});Q12=makeQuery(id+"F0.imprint","IMPRINT",FACE,{"disambiguationData":[TD([[makeQuery(id+"F0.imprint","IMPRINT",EDGE,{"disambiguationData":[TD([[subQ2,-1.0]])],"derivedFrom":subQ1}),1.0]])]});}
            var Q13;
            {var subQ0=sQuery(id+"F0.wireOp",EDGE,"E15.left");var subQ1=sQuery(id+"F0.wireOp",EDGE,"E4.bottom");var subQ2=makeQuery(id+"F0.imprint","INTERSECT",VERTEX,{"derivedFrom":[subQ1,subQ0]});Q13=makeQuery(id+"F0.imprint","IMPRINT",FACE,{"disambiguationData":[TD([[makeQuery(id+"F0.imprint","IMPRINT",EDGE,{"disambiguationData":[TD([[subQ2,-1.0]])],"derivedFrom":subQ1}),1.0]])]});}
            var Q14;
            {var subQ0=sQuery(id+"F0.wireOp",EDGE,"E16.left");var subQ1=sQuery(id+"F0.wireOp",EDGE,"E4.bottom");var subQ2=makeQuery(id+"F0.imprint","INTERSECT",VERTEX,{"derivedFrom":[subQ1,subQ0]});Q14=makeQuery(id+"F0.imprint","IMPRINT",FACE,{"disambiguationData":[TD([[makeQuery(id+"F0.imprint","IMPRINT",EDGE,{"disambiguationData":[TD([[subQ2,-1.0]])],"derivedFrom":subQ1}),1.0]])]});}
            var Q15;
            {var subQ0=sQuery(id+"F0.wireOp",EDGE,"E17.left");var subQ1=sQuery(id+"F0.wireOp",EDGE,"E4.bottom");var subQ2=makeQuery(id+"F0.imprint","INTERSECT",VERTEX,{"derivedFrom":[subQ1,subQ0]});Q15=makeQuery(id+"F0.imprint","IMPRINT",FACE,{"disambiguationData":[TD([[makeQuery(id+"F0.imprint","IMPRINT",EDGE,{"disambiguationData":[TD([[subQ2,-1.0]])],"derivedFrom":subQ1}),1.0]])]});}
            var Q16;
            {var subQ0=sQuery(id+"F0.wireOp",EDGE,"E18.left");var subQ1=sQuery(id+"F0.wireOp",EDGE,"E4.bottom");var subQ2=makeQuery(id+"F0.imprint","INTERSECT",VERTEX,{"derivedFrom":[subQ1,subQ0]});Q16=makeQuery(id+"F0.imprint","IMPRINT",FACE,{"disambiguationData":[TD([[makeQuery(id+"F0.imprint","IMPRINT",EDGE,{"disambiguationData":[TD([[subQ2,-1.0]])],"derivedFrom":subQ1}),1.0]])]});}
            var Q17;
            {var subQ0=sQuery(id+"F0.wireOp",EDGE,"E19.left");var subQ1=sQuery(id+"F0.wireOp",EDGE,"E4.bottom");var subQ2=makeQuery(id+"F0.imprint","INTERSECT",VERTEX,{"derivedFrom":[subQ1,subQ0]});Q17=makeQuery(id+"F0.imprint","IMPRINT",FACE,{"disambiguationData":[TD([[makeQuery(id+"F0.imprint","IMPRINT",EDGE,{"disambiguationData":[TD([[subQ2,-1.0]])],"derivedFrom":subQ1}),1.0]])]});}
            var Q18;
            {var subQ0=sQuery(id+"F0.wireOp",EDGE,"E20.right");var subQ1=sQuery(id+"F0.wireOp",EDGE,"E4.bottom");var subQ2=makeQuery(id+"F0.imprint","INTERSECT",VERTEX,{"derivedFrom":[subQ1,subQ0]});Q18=makeQuery(id+"F0.imprint","IMPRINT",FACE,{"disambiguationData":[TD([[makeQuery(id+"F0.imprint","IMPRINT",EDGE,{"disambiguationData":[TD([[subQ2,-1.0]])],"derivedFrom":subQ1}),-1.0]])]});}
            var Q19;
            {var subQ0=sQuery(id+"F0.wireOp",EDGE,"E21.left");var subQ1=sQuery(id+"F0.wireOp",EDGE,"E4.bottom");var subQ2=makeQuery(id+"F0.imprint","INTERSECT",VERTEX,{"derivedFrom":[subQ1,subQ0]});Q19=makeQuery(id+"F0.imprint","IMPRINT",FACE,{"disambiguationData":[TD([[makeQuery(id+"F0.imprint","IMPRINT",EDGE,{"disambiguationData":[TD([[subQ2,-1.0]])],"derivedFrom":subQ1}),-1.0]])]});}
            var Q20;
            {var subQ0=sQuery(id+"F0.wireOp",EDGE,"E22.left");var subQ1=sQuery(id+"F0.wireOp",EDGE,"E4.bottom");var subQ2=makeQuery(id+"F0.imprint","INTERSECT",VERTEX,{"derivedFrom":[subQ1,subQ0]});Q20=makeQuery(id+"F0.imprint","IMPRINT",FACE,{"disambiguationData":[TD([[makeQuery(id+"F0.imprint","IMPRINT",EDGE,{"disambiguationData":[TD([[subQ2,-1.0]])],"derivedFrom":subQ1}),-1.0]])]});}
            var Q21;
            {var subQ0=sQuery(id+"F0.wireOp",EDGE,"E20.right");var subQ1=sQuery(id+"F0.wireOp",EDGE,"E4.bottom");var subQ2=makeQuery(id+"F0.imprint","INTERSECT",VERTEX,{"derivedFrom":[subQ1,subQ0]});Q21=makeQuery(id+"F0.imprint","IMPRINT",FACE,{"disambiguationData":[TD([[makeQuery(id+"F0.imprint","IMPRINT",EDGE,{"disambiguationData":[TD([[subQ2,-1.0]])],"derivedFrom":subQ1}),1.0]])]});}
            var Q22;
            {var subQ0=sQuery(id+"F0.wireOp",EDGE,"E21.left");var subQ1=sQuery(id+"F0.wireOp",EDGE,"E4.bottom");var subQ2=makeQuery(id+"F0.imprint","INTERSECT",VERTEX,{"derivedFrom":[subQ1,subQ0]});Q22=makeQuery(id+"F0.imprint","IMPRINT",FACE,{"disambiguationData":[TD([[makeQuery(id+"F0.imprint","IMPRINT",EDGE,{"disambiguationData":[TD([[subQ2,-1.0]])],"derivedFrom":subQ1}),1.0]])]});}
            var Q23;
            {var subQ0=sQuery(id+"F0.wireOp",EDGE,"E22.left");var subQ1=sQuery(id+"F0.wireOp",EDGE,"E4.bottom");var subQ2=makeQuery(id+"F0.imprint","INTERSECT",VERTEX,{"derivedFrom":[subQ1,subQ0]});Q23=makeQuery(id+"F0.imprint","IMPRINT",FACE,{"disambiguationData":[TD([[makeQuery(id+"F0.imprint","IMPRINT",EDGE,{"disambiguationData":[TD([[subQ2,-1.0]])],"derivedFrom":subQ1}),1.0]])]});}
            var Q24;
            {var subQ0=sQuery(id+"F0.wireOp",EDGE,"E23.left");var subQ1=sQuery(id+"F0.wireOp",EDGE,"E4.bottom");var subQ2=makeQuery(id+"F0.imprint","INTERSECT",VERTEX,{"derivedFrom":[subQ1,subQ0]});Q24=makeQuery(id+"F0.imprint","IMPRINT",FACE,{"disambiguationData":[TD([[makeQuery(id+"F0.imprint","IMPRINT",EDGE,{"disambiguationData":[TD([[subQ2,-1.0]])],"derivedFrom":subQ1}),-1.0]])]});}
            var Q25;
            {var subQ0=sQuery(id+"F0.wireOp",EDGE,"E25.left");var subQ1=sQuery(id+"F0.wireOp",EDGE,"E4.bottom");var subQ2=makeQuery(id+"F0.imprint","INTERSECT",VERTEX,{"derivedFrom":[subQ1,subQ0]});Q25=makeQuery(id+"F0.imprint","IMPRINT",FACE,{"disambiguationData":[TD([[makeQuery(id+"F0.imprint","IMPRINT",EDGE,{"disambiguationData":[TD([[subQ2,-1.0]])],"derivedFrom":subQ1}),-1.0]])]});}
            var Q26;
            {var subQ0=sQuery(id+"F0.wireOp",EDGE,"E26.left");var subQ1=sQuery(id+"F0.wireOp",EDGE,"E4.bottom");var subQ2=makeQuery(id+"F0.imprint","INTERSECT",VERTEX,{"derivedFrom":[subQ1,subQ0]});Q26=makeQuery(id+"F0.imprint","IMPRINT",FACE,{"disambiguationData":[TD([[makeQuery(id+"F0.imprint","IMPRINT",EDGE,{"disambiguationData":[TD([[subQ2,-1.0]])],"derivedFrom":subQ1}),-1.0]])]});}
            var Q27;
            {var subQ0=sQuery(id+"F0.wireOp",EDGE,"E27.left");var subQ1=sQuery(id+"F0.wireOp",EDGE,"E4.bottom");var subQ2=makeQuery(id+"F0.imprint","INTERSECT",VERTEX,{"derivedFrom":[subQ1,subQ0]});Q27=makeQuery(id+"F0.imprint","IMPRINT",FACE,{"disambiguationData":[TD([[makeQuery(id+"F0.imprint","IMPRINT",EDGE,{"disambiguationData":[TD([[subQ2,-1.0]])],"derivedFrom":subQ1}),-1.0]])]});}
            var Q28;
            {var subQ0=sQuery(id+"F0.wireOp",EDGE,"E28.left");var subQ1=sQuery(id+"F0.wireOp",EDGE,"E4.bottom");var subQ2=makeQuery(id+"F0.imprint","INTERSECT",VERTEX,{"derivedFrom":[subQ1,subQ0]});Q28=makeQuery(id+"F0.imprint","IMPRINT",FACE,{"disambiguationData":[TD([[makeQuery(id+"F0.imprint","IMPRINT",EDGE,{"disambiguationData":[TD([[subQ2,-1.0]])],"derivedFrom":subQ1}),-1.0]])]});}
            var Q29;
            {var subQ0=sQuery(id+"F0.wireOp",EDGE,"E30.right");var subQ1=sQuery(id+"F0.wireOp",EDGE,"E4.bottom");var subQ2=makeQuery(id+"F0.imprint","INTERSECT",VERTEX,{"derivedFrom":[subQ1,subQ0]});Q29=makeQuery(id+"F0.imprint","IMPRINT",FACE,{"disambiguationData":[TD([[makeQuery(id+"F0.imprint","IMPRINT",EDGE,{"disambiguationData":[TD([[subQ2,-1.0]])],"derivedFrom":subQ1}),-1.0]])]});}
            var Q30;
            {var subQ0=sQuery(id+"F0.wireOp",EDGE,"E29.right");var subQ1=sQuery(id+"F0.wireOp",EDGE,"E4.bottom");var subQ2=makeQuery(id+"F0.imprint","INTERSECT",VERTEX,{"derivedFrom":[subQ1,subQ0]});Q30=makeQuery(id+"F0.imprint","IMPRINT",FACE,{"disambiguationData":[TD([[makeQuery(id+"F0.imprint","IMPRINT",EDGE,{"disambiguationData":[TD([[subQ2,-1.0]])],"derivedFrom":subQ1}),-1.0]])]});}
            var Q31;
            {var subQ0=sQuery(id+"F0.wireOp",EDGE,"E29.right");var subQ1=sQuery(id+"F0.wireOp",EDGE,"E4.bottom");var subQ2=makeQuery(id+"F0.imprint","INTERSECT",VERTEX,{"derivedFrom":[subQ1,subQ0]});Q31=makeQuery(id+"F0.imprint","IMPRINT",FACE,{"disambiguationData":[TD([[makeQuery(id+"F0.imprint","IMPRINT",EDGE,{"disambiguationData":[TD([[subQ2,-1.0]])],"derivedFrom":subQ1}),1.0]])]});}
            var Q32;
            {var subQ0=sQuery(id+"F0.wireOp",EDGE,"E30.right");var subQ1=sQuery(id+"F0.wireOp",EDGE,"E0.bottom");var subQ2=makeQuery(id+"F0.imprint","INTERSECT",VERTEX,{"derivedFrom":[subQ1,subQ0]});Q32=makeQuery(id+"F0.imprint","IMPRINT",FACE,{"disambiguationData":[TD([[makeQuery(id+"F0.imprint","IMPRINT",EDGE,{"disambiguationData":[TD([[subQ2,-1.0]])],"derivedFrom":subQ1}),-1.0]])]});}
            var Q33;
            {var subQ0=sQuery(id+"F0.wireOp",EDGE,"E30.right");var subQ1=sQuery(id+"F0.wireOp",EDGE,"E0.top");var subQ2=makeQuery(id+"F0.imprint","INTERSECT",VERTEX,{"derivedFrom":[subQ1,subQ0]});Q33=makeQuery(id+"F0.imprint","IMPRINT",FACE,{"disambiguationData":[TD([[makeQuery(id+"F0.imprint","IMPRINT",EDGE,{"disambiguationData":[TD([[subQ2,-1.0]])],"derivedFrom":subQ1}),1.0]])]});}
            var Q34;
            {var subQ0=sQuery(id+"F0.wireOp",EDGE,"E29.right");var subQ1=sQuery(id+"F0.wireOp",EDGE,"E3.bottom");var subQ2=makeQuery(id+"F0.imprint","INTERSECT",VERTEX,{"derivedFrom":[subQ1,subQ0]});Q34=makeQuery(id+"F0.imprint","IMPRINT",FACE,{"disambiguationData":[TD([[makeQuery(id+"F0.imprint","IMPRINT",EDGE,{"disambiguationData":[TD([[subQ2,-1.0]])],"derivedFrom":subQ1}),1.0]])]});}
            var Q35;
            {var subQ0=sQuery(id+"F0.wireOp",EDGE,"E30.right");var subQ1=sQuery(id+"F0.wireOp",EDGE,"E0.top");var subQ2=makeQuery(id+"F0.imprint","INTERSECT",VERTEX,{"derivedFrom":[subQ1,subQ0]});Q35=makeQuery(id+"F0.imprint","IMPRINT",FACE,{"disambiguationData":[TD([[makeQuery(id+"F0.imprint","IMPRINT",EDGE,{"disambiguationData":[TD([[subQ2,-1.0]])],"derivedFrom":subQ1}),-1.0]])]});}
            var Q36;
            {var subQ0=sQuery(id+"F0.wireOp",EDGE,"E30.right");var subQ1=sQuery(id+"F0.wireOp",EDGE,"E0.bottom");var subQ2=makeQuery(id+"F0.imprint","INTERSECT",VERTEX,{"derivedFrom":[subQ1,subQ0]});Q36=makeQuery(id+"F0.imprint","IMPRINT",FACE,{"disambiguationData":[TD([[makeQuery(id+"F0.imprint","IMPRINT",EDGE,{"disambiguationData":[TD([[subQ2,-1.0]])],"derivedFrom":subQ1}),1.0]])]});}
            var Q37;
            {var subQ0=sQuery(id+"F0.wireOp",EDGE,"E28.left");var subQ1=sQuery(id+"F0.wireOp",EDGE,"E4.bottom");var subQ2=makeQuery(id+"F0.imprint","INTERSECT",VERTEX,{"derivedFrom":[subQ1,subQ0]});Q37=makeQuery(id+"F0.imprint","IMPRINT",FACE,{"disambiguationData":[TD([[makeQuery(id+"F0.imprint","IMPRINT",EDGE,{"disambiguationData":[TD([[subQ2,-1.0]])],"derivedFrom":subQ1}),1.0]])]});}
            var Q38;
            {var subQ0=sQuery(id+"F0.wireOp",EDGE,"E28.left");var subQ1=sQuery(id+"F0.wireOp",EDGE,"E3.bottom");var subQ2=makeQuery(id+"F0.imprint","INTERSECT",VERTEX,{"derivedFrom":[subQ1,subQ0]});Q38=makeQuery(id+"F0.imprint","IMPRINT",FACE,{"disambiguationData":[TD([[makeQuery(id+"F0.imprint","IMPRINT",EDGE,{"disambiguationData":[TD([[subQ2,-1.0]])],"derivedFrom":subQ1}),1.0]])]});}
            var Q39;
            {var subQ0=sQuery(id+"F0.wireOp",EDGE,"E27.left");var subQ1=sQuery(id+"F0.wireOp",EDGE,"E4.bottom");var subQ2=makeQuery(id+"F0.imprint","INTERSECT",VERTEX,{"derivedFrom":[subQ1,subQ0]});Q39=makeQuery(id+"F0.imprint","IMPRINT",FACE,{"disambiguationData":[TD([[makeQuery(id+"F0.imprint","IMPRINT",EDGE,{"disambiguationData":[TD([[subQ2,-1.0]])],"derivedFrom":subQ1}),1.0]])]});}
            var Q40;
            {var subQ0=sQuery(id+"F0.wireOp",EDGE,"E27.left");var subQ1=sQuery(id+"F0.wireOp",EDGE,"E3.bottom");var subQ2=makeQuery(id+"F0.imprint","INTERSECT",VERTEX,{"derivedFrom":[subQ1,subQ0]});Q40=makeQuery(id+"F0.imprint","IMPRINT",FACE,{"disambiguationData":[TD([[makeQuery(id+"F0.imprint","IMPRINT",EDGE,{"disambiguationData":[TD([[subQ2,-1.0]])],"derivedFrom":subQ1}),1.0]])]});}
            var Q41;
            {var subQ0=sQuery(id+"F0.wireOp",EDGE,"E26.left");var subQ1=sQuery(id+"F0.wireOp",EDGE,"E4.bottom");var subQ2=makeQuery(id+"F0.imprint","INTERSECT",VERTEX,{"derivedFrom":[subQ1,subQ0]});Q41=makeQuery(id+"F0.imprint","IMPRINT",FACE,{"disambiguationData":[TD([[makeQuery(id+"F0.imprint","IMPRINT",EDGE,{"disambiguationData":[TD([[subQ2,-1.0]])],"derivedFrom":subQ1}),1.0]])]});}
            var Q42;
            {var subQ0=sQuery(id+"F0.wireOp",EDGE,"E26.left");var subQ1=sQuery(id+"F0.wireOp",EDGE,"E3.bottom");var subQ2=makeQuery(id+"F0.imprint","INTERSECT",VERTEX,{"derivedFrom":[subQ1,subQ0]});Q42=makeQuery(id+"F0.imprint","IMPRINT",FACE,{"disambiguationData":[TD([[makeQuery(id+"F0.imprint","IMPRINT",EDGE,{"disambiguationData":[TD([[subQ2,-1.0]])],"derivedFrom":subQ1}),1.0]])]});}
            var Q43;
            {var subQ0=sQuery(id+"F0.wireOp",EDGE,"E25.left");var subQ1=sQuery(id+"F0.wireOp",EDGE,"E3.bottom");var subQ2=makeQuery(id+"F0.imprint","INTERSECT",VERTEX,{"derivedFrom":[subQ1,subQ0]});Q43=makeQuery(id+"F0.imprint","IMPRINT",FACE,{"disambiguationData":[TD([[makeQuery(id+"F0.imprint","IMPRINT",EDGE,{"disambiguationData":[TD([[subQ2,-1.0]])],"derivedFrom":subQ1}),1.0]])]});}
            var Q44;
            {var subQ0=sQuery(id+"F0.wireOp",EDGE,"E25.left");var subQ1=sQuery(id+"F0.wireOp",EDGE,"E4.bottom");var subQ2=makeQuery(id+"F0.imprint","INTERSECT",VERTEX,{"derivedFrom":[subQ1,subQ0]});Q44=makeQuery(id+"F0.imprint","IMPRINT",FACE,{"disambiguationData":[TD([[makeQuery(id+"F0.imprint","IMPRINT",EDGE,{"disambiguationData":[TD([[subQ2,-1.0]])],"derivedFrom":subQ1}),1.0]])]});}
            var Q45;
            {var subQ0=sQuery(id+"F0.wireOp",EDGE,"E23.left");var subQ1=sQuery(id+"F0.wireOp",EDGE,"E4.bottom");var subQ2=makeQuery(id+"F0.imprint","INTERSECT",VERTEX,{"derivedFrom":[subQ1,subQ0]});Q45=makeQuery(id+"F0.imprint","IMPRINT",FACE,{"disambiguationData":[TD([[makeQuery(id+"F0.imprint","IMPRINT",EDGE,{"disambiguationData":[TD([[subQ2,-1.0]])],"derivedFrom":subQ1}),1.0]])]});}
            var Q46;
            {var subQ0=sQuery(id+"F0.wireOp",EDGE,"E23.left");var subQ1=sQuery(id+"F0.wireOp",EDGE,"E3.bottom");var subQ2=makeQuery(id+"F0.imprint","INTERSECT",VERTEX,{"derivedFrom":[subQ1,subQ0]});Q46=makeQuery(id+"F0.imprint","IMPRINT",FACE,{"disambiguationData":[TD([[makeQuery(id+"F0.imprint","IMPRINT",EDGE,{"disambiguationData":[TD([[subQ2,-1.0]])],"derivedFrom":subQ1}),1.0]])]});}
            var Q47;
            {var subQ0=sQuery(id+"F0.wireOp",EDGE,"E22.left");var subQ1=sQuery(id+"F0.wireOp",EDGE,"E3.bottom");var subQ2=makeQuery(id+"F0.imprint","INTERSECT",VERTEX,{"derivedFrom":[subQ1,subQ0]});Q47=makeQuery(id+"F0.imprint","IMPRINT",FACE,{"disambiguationData":[TD([[makeQuery(id+"F0.imprint","IMPRINT",EDGE,{"disambiguationData":[TD([[subQ2,-1.0]])],"derivedFrom":subQ1}),1.0]])]});}
            var Q48;
            {var subQ0=sQuery(id+"F0.wireOp",EDGE,"E21.left");var subQ1=sQuery(id+"F0.wireOp",EDGE,"E3.bottom");var subQ2=makeQuery(id+"F0.imprint","INTERSECT",VERTEX,{"derivedFrom":[subQ1,subQ0]});Q48=makeQuery(id+"F0.imprint","IMPRINT",FACE,{"disambiguationData":[TD([[makeQuery(id+"F0.imprint","IMPRINT",EDGE,{"disambiguationData":[TD([[subQ2,-1.0]])],"derivedFrom":subQ1}),1.0]])]});}
            var Q49;
            {var subQ0=sQuery(id+"F0.wireOp",EDGE,"E20.right");var subQ1=sQuery(id+"F0.wireOp",EDGE,"E3.bottom");var subQ2=makeQuery(id+"F0.imprint","INTERSECT",VERTEX,{"derivedFrom":[subQ1,subQ0]});Q49=makeQuery(id+"F0.imprint","IMPRINT",FACE,{"disambiguationData":[TD([[makeQuery(id+"F0.imprint","IMPRINT",EDGE,{"disambiguationData":[TD([[subQ2,-1.0]])],"derivedFrom":subQ1}),1.0]])]});}
            var Q50;
            {var subQ0=sQuery(id+"F0.wireOp",EDGE,"E19.left");var subQ1=sQuery(id+"F0.wireOp",EDGE,"E3.bottom");var subQ2=makeQuery(id+"F0.imprint","INTERSECT",VERTEX,{"derivedFrom":[subQ1,subQ0]});Q50=makeQuery(id+"F0.imprint","IMPRINT",FACE,{"disambiguationData":[TD([[makeQuery(id+"F0.imprint","IMPRINT",EDGE,{"disambiguationData":[TD([[subQ2,-1.0]])],"derivedFrom":subQ1}),1.0]])]});}
            var Q51;
            {var subQ0=sQuery(id+"F0.wireOp",EDGE,"E19.left");var subQ1=sQuery(id+"F0.wireOp",EDGE,"E2.bottom");var subQ2=makeQuery(id+"F0.imprint","INTERSECT",VERTEX,{"derivedFrom":[subQ1,subQ0]});Q51=makeQuery(id+"F0.imprint","IMPRINT",FACE,{"disambiguationData":[TD([[makeQuery(id+"F0.imprint","IMPRINT",EDGE,{"disambiguationData":[TD([[subQ2,-1.0]])],"derivedFrom":subQ1}),1.0]])]});}
            var Q52;
            {var subQ0=sQuery(id+"F0.wireOp",EDGE,"E20.right");var subQ1=sQuery(id+"F0.wireOp",EDGE,"E2.bottom");var subQ2=makeQuery(id+"F0.imprint","INTERSECT",VERTEX,{"derivedFrom":[subQ1,subQ0]});Q52=makeQuery(id+"F0.imprint","IMPRINT",FACE,{"disambiguationData":[TD([[makeQuery(id+"F0.imprint","IMPRINT",EDGE,{"disambiguationData":[TD([[subQ2,-1.0]])],"derivedFrom":subQ1}),1.0]])]});}
            var Q53;
            {var subQ0=sQuery(id+"F0.wireOp",EDGE,"E21.left");var subQ1=sQuery(id+"F0.wireOp",EDGE,"E2.bottom");var subQ2=makeQuery(id+"F0.imprint","INTERSECT",VERTEX,{"derivedFrom":[subQ1,subQ0]});Q53=makeQuery(id+"F0.imprint","IMPRINT",FACE,{"disambiguationData":[TD([[makeQuery(id+"F0.imprint","IMPRINT",EDGE,{"disambiguationData":[TD([[subQ2,-1.0]])],"derivedFrom":subQ1}),1.0]])]});}
            var Q54;
            {var subQ0=sQuery(id+"F0.wireOp",EDGE,"E22.left");var subQ1=sQuery(id+"F0.wireOp",EDGE,"E2.bottom");var subQ2=makeQuery(id+"F0.imprint","INTERSECT",VERTEX,{"derivedFrom":[subQ1,subQ0]});Q54=makeQuery(id+"F0.imprint","IMPRINT",FACE,{"disambiguationData":[TD([[makeQuery(id+"F0.imprint","IMPRINT",EDGE,{"disambiguationData":[TD([[subQ2,-1.0]])],"derivedFrom":subQ1}),1.0]])]});}
            var Q55;
            {var subQ0=sQuery(id+"F0.wireOp",EDGE,"E23.left");var subQ1=sQuery(id+"F0.wireOp",EDGE,"E2.bottom");var subQ2=makeQuery(id+"F0.imprint","INTERSECT",VERTEX,{"derivedFrom":[subQ1,subQ0]});Q55=makeQuery(id+"F0.imprint","IMPRINT",FACE,{"disambiguationData":[TD([[makeQuery(id+"F0.imprint","IMPRINT",EDGE,{"disambiguationData":[TD([[subQ2,-1.0]])],"derivedFrom":subQ1}),1.0]])]});}
            var Q56;
            {var subQ0=sQuery(id+"F0.wireOp",EDGE,"E25.left");var subQ1=sQuery(id+"F0.wireOp",EDGE,"E2.bottom");var subQ2=makeQuery(id+"F0.imprint","INTERSECT",VERTEX,{"derivedFrom":[subQ1,subQ0]});Q56=makeQuery(id+"F0.imprint","IMPRINT",FACE,{"disambiguationData":[TD([[makeQuery(id+"F0.imprint","IMPRINT",EDGE,{"disambiguationData":[TD([[subQ2,-1.0]])],"derivedFrom":subQ1}),1.0]])]});}
            var Q57;
            {var subQ0=sQuery(id+"F0.wireOp",EDGE,"E25.left");var subQ1=sQuery(id+"F0.wireOp",EDGE,"E1.bottom");var subQ2=makeQuery(id+"F0.imprint","INTERSECT",VERTEX,{"derivedFrom":[subQ1,subQ0]});Q57=makeQuery(id+"F0.imprint","IMPRINT",FACE,{"disambiguationData":[TD([[makeQuery(id+"F0.imprint","IMPRINT",EDGE,{"disambiguationData":[TD([[subQ2,-1.0]])],"derivedFrom":subQ1}),1.0]])]});}
            var Q58;
            {var subQ0=sQuery(id+"F0.wireOp",EDGE,"E26.left");var subQ1=sQuery(id+"F0.wireOp",EDGE,"E2.bottom");var subQ2=makeQuery(id+"F0.imprint","INTERSECT",VERTEX,{"derivedFrom":[subQ1,subQ0]});Q58=makeQuery(id+"F0.imprint","IMPRINT",FACE,{"disambiguationData":[TD([[makeQuery(id+"F0.imprint","IMPRINT",EDGE,{"disambiguationData":[TD([[subQ2,-1.0]])],"derivedFrom":subQ1}),1.0]])]});}
            var Q59;
            {var subQ0=sQuery(id+"F0.wireOp",EDGE,"E26.left");var subQ1=sQuery(id+"F0.wireOp",EDGE,"E1.bottom");var subQ2=makeQuery(id+"F0.imprint","INTERSECT",VERTEX,{"derivedFrom":[subQ1,subQ0]});Q59=makeQuery(id+"F0.imprint","IMPRINT",FACE,{"disambiguationData":[TD([[makeQuery(id+"F0.imprint","IMPRINT",EDGE,{"disambiguationData":[TD([[subQ2,-1.0]])],"derivedFrom":subQ1}),1.0]])]});}
            var Q60;
            {var subQ0=sQuery(id+"F0.wireOp",EDGE,"E27.left");var subQ1=sQuery(id+"F0.wireOp",EDGE,"E2.bottom");var subQ2=makeQuery(id+"F0.imprint","INTERSECT",VERTEX,{"derivedFrom":[subQ1,subQ0]});Q60=makeQuery(id+"F0.imprint","IMPRINT",FACE,{"disambiguationData":[TD([[makeQuery(id+"F0.imprint","IMPRINT",EDGE,{"disambiguationData":[TD([[subQ2,-1.0]])],"derivedFrom":subQ1}),1.0]])]});}
            var Q61;
            {var subQ0=sQuery(id+"F0.wireOp",EDGE,"E27.left");var subQ1=sQuery(id+"F0.wireOp",EDGE,"E1.bottom");var subQ2=makeQuery(id+"F0.imprint","INTERSECT",VERTEX,{"derivedFrom":[subQ1,subQ0]});Q61=makeQuery(id+"F0.imprint","IMPRINT",FACE,{"disambiguationData":[TD([[makeQuery(id+"F0.imprint","IMPRINT",EDGE,{"disambiguationData":[TD([[subQ2,-1.0]])],"derivedFrom":subQ1}),1.0]])]});}
            var Q62;
            {var subQ0=sQuery(id+"F0.wireOp",EDGE,"E28.left");var subQ1=sQuery(id+"F0.wireOp",EDGE,"E2.bottom");var subQ2=makeQuery(id+"F0.imprint","INTERSECT",VERTEX,{"derivedFrom":[subQ1,subQ0]});Q62=makeQuery(id+"F0.imprint","IMPRINT",FACE,{"disambiguationData":[TD([[makeQuery(id+"F0.imprint","IMPRINT",EDGE,{"disambiguationData":[TD([[subQ2,-1.0]])],"derivedFrom":subQ1}),1.0]])]});}
            var Q63;
            {var subQ0=sQuery(id+"F0.wireOp",EDGE,"E28.left");var subQ1=sQuery(id+"F0.wireOp",EDGE,"E1.bottom");var subQ2=makeQuery(id+"F0.imprint","INTERSECT",VERTEX,{"derivedFrom":[subQ1,subQ0]});Q63=makeQuery(id+"F0.imprint","IMPRINT",FACE,{"disambiguationData":[TD([[makeQuery(id+"F0.imprint","IMPRINT",EDGE,{"disambiguationData":[TD([[subQ2,-1.0]])],"derivedFrom":subQ1}),1.0]])]});}
            var Q64;
            {var subQ0=sQuery(id+"F0.wireOp",EDGE,"E29.right");var subQ1=sQuery(id+"F0.wireOp",EDGE,"E2.bottom");var subQ2=makeQuery(id+"F0.imprint","INTERSECT",VERTEX,{"derivedFrom":[subQ1,subQ0]});Q64=makeQuery(id+"F0.imprint","IMPRINT",FACE,{"disambiguationData":[TD([[makeQuery(id+"F0.imprint","IMPRINT",EDGE,{"disambiguationData":[TD([[subQ2,-1.0]])],"derivedFrom":subQ1}),1.0]])]});}
            var Q65;
            {var subQ0=sQuery(id+"F0.wireOp",EDGE,"E29.right");var subQ1=sQuery(id+"F0.wireOp",EDGE,"E1.bottom");var subQ2=makeQuery(id+"F0.imprint","INTERSECT",VERTEX,{"derivedFrom":[subQ1,subQ0]});Q65=makeQuery(id+"F0.imprint","IMPRINT",FACE,{"disambiguationData":[TD([[makeQuery(id+"F0.imprint","IMPRINT",EDGE,{"disambiguationData":[TD([[subQ2,-1.0]])],"derivedFrom":subQ1}),1.0]])]});}
            var Q66;
            {var subQ0=sQuery(id+"F0.wireOp",EDGE,"E30.right");var subQ1=sQuery(id+"F0.wireOp",EDGE,"E2.bottom");var subQ2=makeQuery(id+"F0.imprint","INTERSECT",VERTEX,{"derivedFrom":[subQ1,subQ0]});Q66=makeQuery(id+"F0.imprint","IMPRINT",FACE,{"disambiguationData":[TD([[makeQuery(id+"F0.imprint","IMPRINT",EDGE,{"disambiguationData":[TD([[subQ2,-1.0]])],"derivedFrom":subQ1}),1.0]])]});}
            var Q67;
            {var subQ0=sQuery(id+"F0.wireOp",EDGE,"E30.right");var subQ1=sQuery(id+"F0.wireOp",EDGE,"E1.bottom");var subQ2=makeQuery(id+"F0.imprint","INTERSECT",VERTEX,{"derivedFrom":[subQ1,subQ0]});Q67=makeQuery(id+"F0.imprint","IMPRINT",FACE,{"disambiguationData":[TD([[makeQuery(id+"F0.imprint","IMPRINT",EDGE,{"disambiguationData":[TD([[subQ2,-1.0]])],"derivedFrom":subQ1}),1.0]])]});}
            var Q68;
            {var subQ0=sQuery(id+"F0.wireOp",EDGE,"E30.right");var subQ1=sQuery(id+"F0.wireOp",EDGE,"E7.bottom");var subQ2=makeQuery(id+"F0.imprint","INTERSECT",VERTEX,{"derivedFrom":[subQ1,subQ0]});Q68=makeQuery(id+"F0.imprint","IMPRINT",FACE,{"disambiguationData":[TD([[makeQuery(id+"F0.imprint","IMPRINT",EDGE,{"disambiguationData":[TD([[subQ2,-1.0]])],"derivedFrom":subQ1}),1.0]])]});}
            var Q69;
            {var subQ0=sQuery(id+"F0.wireOp",EDGE,"E30.right");var subQ1=sQuery(id+"F0.wireOp",EDGE,"E6.bottom");var subQ2=makeQuery(id+"F0.imprint","INTERSECT",VERTEX,{"derivedFrom":[subQ1,subQ0]});Q69=makeQuery(id+"F0.imprint","IMPRINT",FACE,{"disambiguationData":[TD([[makeQuery(id+"F0.imprint","IMPRINT",EDGE,{"disambiguationData":[TD([[subQ2,-1.0]])],"derivedFrom":subQ1}),1.0]])]});}
            var Q70;
            {var subQ0=sQuery(id+"F0.wireOp",EDGE,"E30.right");var subQ1=sQuery(id+"F0.wireOp",EDGE,"E5.bottom");var subQ2=makeQuery(id+"F0.imprint","INTERSECT",VERTEX,{"derivedFrom":[subQ1,subQ0]});Q70=makeQuery(id+"F0.imprint","IMPRINT",FACE,{"disambiguationData":[TD([[makeQuery(id+"F0.imprint","IMPRINT",EDGE,{"disambiguationData":[TD([[subQ2,-1.0]])],"derivedFrom":subQ1}),1.0]])]});}
            var Q71;
            {var subQ0=sQuery(id+"F0.wireOp",EDGE,"E29.right");var subQ1=sQuery(id+"F0.wireOp",EDGE,"E5.bottom");var subQ2=makeQuery(id+"F0.imprint","INTERSECT",VERTEX,{"derivedFrom":[subQ1,subQ0]});Q71=makeQuery(id+"F0.imprint","IMPRINT",FACE,{"disambiguationData":[TD([[makeQuery(id+"F0.imprint","IMPRINT",EDGE,{"disambiguationData":[TD([[subQ2,-1.0]])],"derivedFrom":subQ1}),1.0]])]});}
            var Q72;
            {var subQ0=sQuery(id+"F0.wireOp",EDGE,"E29.right");var subQ1=sQuery(id+"F0.wireOp",EDGE,"E6.bottom");var subQ2=makeQuery(id+"F0.imprint","INTERSECT",VERTEX,{"derivedFrom":[subQ1,subQ0]});Q72=makeQuery(id+"F0.imprint","IMPRINT",FACE,{"disambiguationData":[TD([[makeQuery(id+"F0.imprint","IMPRINT",EDGE,{"disambiguationData":[TD([[subQ2,-1.0]])],"derivedFrom":subQ1}),1.0]])]});}
            var Q73;
            {var subQ0=sQuery(id+"F0.wireOp",EDGE,"E29.right");var subQ1=sQuery(id+"F0.wireOp",EDGE,"E7.bottom");var subQ2=makeQuery(id+"F0.imprint","INTERSECT",VERTEX,{"derivedFrom":[subQ1,subQ0]});Q73=makeQuery(id+"F0.imprint","IMPRINT",FACE,{"disambiguationData":[TD([[makeQuery(id+"F0.imprint","IMPRINT",EDGE,{"disambiguationData":[TD([[subQ2,-1.0]])],"derivedFrom":subQ1}),1.0]])]});}
            var Q74;
            {var subQ0=sQuery(id+"F0.wireOp",EDGE,"E28.left");var subQ1=sQuery(id+"F0.wireOp",EDGE,"E7.bottom");var subQ2=makeQuery(id+"F0.imprint","INTERSECT",VERTEX,{"derivedFrom":[subQ1,subQ0]});Q74=makeQuery(id+"F0.imprint","IMPRINT",FACE,{"disambiguationData":[TD([[makeQuery(id+"F0.imprint","IMPRINT",EDGE,{"disambiguationData":[TD([[subQ2,-1.0]])],"derivedFrom":subQ1}),1.0]])]});}
            var Q75;
            {var subQ0=sQuery(id+"F0.wireOp",EDGE,"E28.left");var subQ1=sQuery(id+"F0.wireOp",EDGE,"E6.bottom");var subQ2=makeQuery(id+"F0.imprint","INTERSECT",VERTEX,{"derivedFrom":[subQ1,subQ0]});Q75=makeQuery(id+"F0.imprint","IMPRINT",FACE,{"disambiguationData":[TD([[makeQuery(id+"F0.imprint","IMPRINT",EDGE,{"disambiguationData":[TD([[subQ2,-1.0]])],"derivedFrom":subQ1}),1.0]])]});}
            var Q76;
            {var subQ0=sQuery(id+"F0.wireOp",EDGE,"E28.left");var subQ1=sQuery(id+"F0.wireOp",EDGE,"E5.bottom");var subQ2=makeQuery(id+"F0.imprint","INTERSECT",VERTEX,{"derivedFrom":[subQ1,subQ0]});Q76=makeQuery(id+"F0.imprint","IMPRINT",FACE,{"disambiguationData":[TD([[makeQuery(id+"F0.imprint","IMPRINT",EDGE,{"disambiguationData":[TD([[subQ2,-1.0]])],"derivedFrom":subQ1}),1.0]])]});}
            var Q77;
            {var subQ0=sQuery(id+"F0.wireOp",EDGE,"E27.left");var subQ1=sQuery(id+"F0.wireOp",EDGE,"E5.bottom");var subQ2=makeQuery(id+"F0.imprint","INTERSECT",VERTEX,{"derivedFrom":[subQ1,subQ0]});Q77=makeQuery(id+"F0.imprint","IMPRINT",FACE,{"disambiguationData":[TD([[makeQuery(id+"F0.imprint","IMPRINT",EDGE,{"disambiguationData":[TD([[subQ2,-1.0]])],"derivedFrom":subQ1}),1.0]])]});}
            var Q78;
            {var subQ0=sQuery(id+"F0.wireOp",EDGE,"E27.left");var subQ1=sQuery(id+"F0.wireOp",EDGE,"E6.bottom");var subQ2=makeQuery(id+"F0.imprint","INTERSECT",VERTEX,{"derivedFrom":[subQ1,subQ0]});Q78=makeQuery(id+"F0.imprint","IMPRINT",FACE,{"disambiguationData":[TD([[makeQuery(id+"F0.imprint","IMPRINT",EDGE,{"disambiguationData":[TD([[subQ2,-1.0]])],"derivedFrom":subQ1}),1.0]])]});}
            var Q79;
            {var subQ0=sQuery(id+"F0.wireOp",EDGE,"E27.left");var subQ1=sQuery(id+"F0.wireOp",EDGE,"E7.bottom");var subQ2=makeQuery(id+"F0.imprint","INTERSECT",VERTEX,{"derivedFrom":[subQ1,subQ0]});Q79=makeQuery(id+"F0.imprint","IMPRINT",FACE,{"disambiguationData":[TD([[makeQuery(id+"F0.imprint","IMPRINT",EDGE,{"disambiguationData":[TD([[subQ2,-1.0]])],"derivedFrom":subQ1}),1.0]])]});}
            var Q80;
            {var subQ0=sQuery(id+"F0.wireOp",EDGE,"E25.left");var subQ1=sQuery(id+"F0.wireOp",EDGE,"E7.bottom");var subQ2=makeQuery(id+"F0.imprint","INTERSECT",VERTEX,{"derivedFrom":[subQ1,subQ0]});Q80=makeQuery(id+"F0.imprint","IMPRINT",FACE,{"disambiguationData":[TD([[makeQuery(id+"F0.imprint","IMPRINT",EDGE,{"disambiguationData":[TD([[subQ2,-1.0]])],"derivedFrom":subQ1}),1.0]])]});}
            var Q81;
            {var subQ0=sQuery(id+"F0.wireOp",EDGE,"E26.left");var subQ1=sQuery(id+"F0.wireOp",EDGE,"E7.bottom");var subQ2=makeQuery(id+"F0.imprint","INTERSECT",VERTEX,{"derivedFrom":[subQ1,subQ0]});Q81=makeQuery(id+"F0.imprint","IMPRINT",FACE,{"disambiguationData":[TD([[makeQuery(id+"F0.imprint","IMPRINT",EDGE,{"disambiguationData":[TD([[subQ2,-1.0]])],"derivedFrom":subQ1}),1.0]])]});}
            var Q82;
            {var subQ0=sQuery(id+"F0.wireOp",EDGE,"E26.left");var subQ1=sQuery(id+"F0.wireOp",EDGE,"E6.bottom");var subQ2=makeQuery(id+"F0.imprint","INTERSECT",VERTEX,{"derivedFrom":[subQ1,subQ0]});Q82=makeQuery(id+"F0.imprint","IMPRINT",FACE,{"disambiguationData":[TD([[makeQuery(id+"F0.imprint","IMPRINT",EDGE,{"disambiguationData":[TD([[subQ2,-1.0]])],"derivedFrom":subQ1}),1.0]])]});}
            var Q83;
            {var subQ0=sQuery(id+"F0.wireOp",EDGE,"E25.left");var subQ1=sQuery(id+"F0.wireOp",EDGE,"E6.bottom");var subQ2=makeQuery(id+"F0.imprint","INTERSECT",VERTEX,{"derivedFrom":[subQ1,subQ0]});Q83=makeQuery(id+"F0.imprint","IMPRINT",FACE,{"disambiguationData":[TD([[makeQuery(id+"F0.imprint","IMPRINT",EDGE,{"disambiguationData":[TD([[subQ2,-1.0]])],"derivedFrom":subQ1}),1.0]])]});}
            var Q84;
            {var subQ0=sQuery(id+"F0.wireOp",EDGE,"E25.left");var subQ1=sQuery(id+"F0.wireOp",EDGE,"E5.bottom");var subQ2=makeQuery(id+"F0.imprint","INTERSECT",VERTEX,{"derivedFrom":[subQ1,subQ0]});Q84=makeQuery(id+"F0.imprint","IMPRINT",FACE,{"disambiguationData":[TD([[makeQuery(id+"F0.imprint","IMPRINT",EDGE,{"disambiguationData":[TD([[subQ2,-1.0]])],"derivedFrom":subQ1}),1.0]])]});}
            var Q85;
            {var subQ0=sQuery(id+"F0.wireOp",EDGE,"E26.left");var subQ1=sQuery(id+"F0.wireOp",EDGE,"E5.bottom");var subQ2=makeQuery(id+"F0.imprint","INTERSECT",VERTEX,{"derivedFrom":[subQ1,subQ0]});Q85=makeQuery(id+"F0.imprint","IMPRINT",FACE,{"disambiguationData":[TD([[makeQuery(id+"F0.imprint","IMPRINT",EDGE,{"disambiguationData":[TD([[subQ2,-1.0]])],"derivedFrom":subQ1}),1.0]])]});}
            var Q86;
            {var subQ0=sQuery(id+"F0.wireOp",EDGE,"E23.left");var subQ1=sQuery(id+"F0.wireOp",EDGE,"E5.bottom");var subQ2=makeQuery(id+"F0.imprint","INTERSECT",VERTEX,{"derivedFrom":[subQ1,subQ0]});Q86=makeQuery(id+"F0.imprint","IMPRINT",FACE,{"disambiguationData":[TD([[makeQuery(id+"F0.imprint","IMPRINT",EDGE,{"disambiguationData":[TD([[subQ2,-1.0]])],"derivedFrom":subQ1}),1.0]])]});}
            var Q87;
            {var subQ0=sQuery(id+"F0.wireOp",EDGE,"E23.left");var subQ1=sQuery(id+"F0.wireOp",EDGE,"E6.bottom");var subQ2=makeQuery(id+"F0.imprint","INTERSECT",VERTEX,{"derivedFrom":[subQ1,subQ0]});Q87=makeQuery(id+"F0.imprint","IMPRINT",FACE,{"disambiguationData":[TD([[makeQuery(id+"F0.imprint","IMPRINT",EDGE,{"disambiguationData":[TD([[subQ2,-1.0]])],"derivedFrom":subQ1}),1.0]])]});}
            var Q88;
            {var subQ0=sQuery(id+"F0.wireOp",EDGE,"E23.left");var subQ1=sQuery(id+"F0.wireOp",EDGE,"E7.bottom");var subQ2=makeQuery(id+"F0.imprint","INTERSECT",VERTEX,{"derivedFrom":[subQ1,subQ0]});Q88=makeQuery(id+"F0.imprint","IMPRINT",FACE,{"disambiguationData":[TD([[makeQuery(id+"F0.imprint","IMPRINT",EDGE,{"disambiguationData":[TD([[subQ2,-1.0]])],"derivedFrom":subQ1}),1.0]])]});}
            var Q89;
            {var subQ0=sQuery(id+"F0.wireOp",EDGE,"E21.left");var subQ1=sQuery(id+"F0.wireOp",EDGE,"E5.bottom");var subQ2=makeQuery(id+"F0.imprint","INTERSECT",VERTEX,{"derivedFrom":[subQ1,subQ0]});Q89=makeQuery(id+"F0.imprint","IMPRINT",FACE,{"disambiguationData":[TD([[makeQuery(id+"F0.imprint","IMPRINT",EDGE,{"disambiguationData":[TD([[subQ2,-1.0]])],"derivedFrom":subQ1}),1.0]])]});}
            var Q90;
            {var subQ0=sQuery(id+"F0.wireOp",EDGE,"E21.left");var subQ1=sQuery(id+"F0.wireOp",EDGE,"E6.bottom");var subQ2=makeQuery(id+"F0.imprint","INTERSECT",VERTEX,{"derivedFrom":[subQ1,subQ0]});Q90=makeQuery(id+"F0.imprint","IMPRINT",FACE,{"disambiguationData":[TD([[makeQuery(id+"F0.imprint","IMPRINT",EDGE,{"disambiguationData":[TD([[subQ2,-1.0]])],"derivedFrom":subQ1}),1.0]])]});}
            var Q91;
            {var subQ0=sQuery(id+"F0.wireOp",EDGE,"E21.left");var subQ1=sQuery(id+"F0.wireOp",EDGE,"E7.bottom");var subQ2=makeQuery(id+"F0.imprint","INTERSECT",VERTEX,{"derivedFrom":[subQ1,subQ0]});Q91=makeQuery(id+"F0.imprint","IMPRINT",FACE,{"disambiguationData":[TD([[makeQuery(id+"F0.imprint","IMPRINT",EDGE,{"disambiguationData":[TD([[subQ2,-1.0]])],"derivedFrom":subQ1}),1.0]])]});}
            var Q92;
            {var subQ0=sQuery(id+"F0.wireOp",EDGE,"E22.left");var subQ1=sQuery(id+"F0.wireOp",EDGE,"E7.bottom");var subQ2=makeQuery(id+"F0.imprint","INTERSECT",VERTEX,{"derivedFrom":[subQ1,subQ0]});Q92=makeQuery(id+"F0.imprint","IMPRINT",FACE,{"disambiguationData":[TD([[makeQuery(id+"F0.imprint","IMPRINT",EDGE,{"disambiguationData":[TD([[subQ2,-1.0]])],"derivedFrom":subQ1}),1.0]])]});}
            var Q93;
            {var subQ0=sQuery(id+"F0.wireOp",EDGE,"E22.left");var subQ1=sQuery(id+"F0.wireOp",EDGE,"E6.bottom");var subQ2=makeQuery(id+"F0.imprint","INTERSECT",VERTEX,{"derivedFrom":[subQ1,subQ0]});Q93=makeQuery(id+"F0.imprint","IMPRINT",FACE,{"disambiguationData":[TD([[makeQuery(id+"F0.imprint","IMPRINT",EDGE,{"disambiguationData":[TD([[subQ2,-1.0]])],"derivedFrom":subQ1}),1.0]])]});}
            var Q94;
            {var subQ0=sQuery(id+"F0.wireOp",EDGE,"E22.left");var subQ1=sQuery(id+"F0.wireOp",EDGE,"E5.bottom");var subQ2=makeQuery(id+"F0.imprint","INTERSECT",VERTEX,{"derivedFrom":[subQ1,subQ0]});Q94=makeQuery(id+"F0.imprint","IMPRINT",FACE,{"disambiguationData":[TD([[makeQuery(id+"F0.imprint","IMPRINT",EDGE,{"disambiguationData":[TD([[subQ2,-1.0]])],"derivedFrom":subQ1}),1.0]])]});}
            var Q95;
            {var subQ0=sQuery(id+"F0.wireOp",EDGE,"E19.left");var subQ1=sQuery(id+"F0.wireOp",EDGE,"E7.bottom");var subQ2=makeQuery(id+"F0.imprint","INTERSECT",VERTEX,{"derivedFrom":[subQ1,subQ0]});Q95=makeQuery(id+"F0.imprint","IMPRINT",FACE,{"disambiguationData":[TD([[makeQuery(id+"F0.imprint","IMPRINT",EDGE,{"disambiguationData":[TD([[subQ2,-1.0]])],"derivedFrom":subQ1}),1.0]])]});}
            var Q96;
            {var subQ0=sQuery(id+"F0.wireOp",EDGE,"E20.right");var subQ1=sQuery(id+"F0.wireOp",EDGE,"E7.bottom");var subQ2=makeQuery(id+"F0.imprint","INTERSECT",VERTEX,{"derivedFrom":[subQ1,subQ0]});Q96=makeQuery(id+"F0.imprint","IMPRINT",FACE,{"disambiguationData":[TD([[makeQuery(id+"F0.imprint","IMPRINT",EDGE,{"disambiguationData":[TD([[subQ2,-1.0]])],"derivedFrom":subQ1}),1.0]])]});}
            var Q97;
            {var subQ0=sQuery(id+"F0.wireOp",EDGE,"E20.right");var subQ1=sQuery(id+"F0.wireOp",EDGE,"E6.bottom");var subQ2=makeQuery(id+"F0.imprint","INTERSECT",VERTEX,{"derivedFrom":[subQ1,subQ0]});Q97=makeQuery(id+"F0.imprint","IMPRINT",FACE,{"disambiguationData":[TD([[makeQuery(id+"F0.imprint","IMPRINT",EDGE,{"disambiguationData":[TD([[subQ2,-1.0]])],"derivedFrom":subQ1}),1.0]])]});}
            var Q98;
            {var subQ0=sQuery(id+"F0.wireOp",EDGE,"E19.left");var subQ1=sQuery(id+"F0.wireOp",EDGE,"E6.bottom");var subQ2=makeQuery(id+"F0.imprint","INTERSECT",VERTEX,{"derivedFrom":[subQ1,subQ0]});Q98=makeQuery(id+"F0.imprint","IMPRINT",FACE,{"disambiguationData":[TD([[makeQuery(id+"F0.imprint","IMPRINT",EDGE,{"disambiguationData":[TD([[subQ2,-1.0]])],"derivedFrom":subQ1}),1.0]])]});}
            var Q99;
            {var subQ0=sQuery(id+"F0.wireOp",EDGE,"E19.left");var subQ1=sQuery(id+"F0.wireOp",EDGE,"E5.bottom");var subQ2=makeQuery(id+"F0.imprint","INTERSECT",VERTEX,{"derivedFrom":[subQ1,subQ0]});Q99=makeQuery(id+"F0.imprint","IMPRINT",FACE,{"disambiguationData":[TD([[makeQuery(id+"F0.imprint","IMPRINT",EDGE,{"disambiguationData":[TD([[subQ2,-1.0]])],"derivedFrom":subQ1}),1.0]])]});}
            var Q100;
            {var subQ0=sQuery(id+"F0.wireOp",EDGE,"E20.right");var subQ1=sQuery(id+"F0.wireOp",EDGE,"E5.bottom");var subQ2=makeQuery(id+"F0.imprint","INTERSECT",VERTEX,{"derivedFrom":[subQ1,subQ0]});Q100=makeQuery(id+"F0.imprint","IMPRINT",FACE,{"disambiguationData":[TD([[makeQuery(id+"F0.imprint","IMPRINT",EDGE,{"disambiguationData":[TD([[subQ2,-1.0]])],"derivedFrom":subQ1}),1.0]])]});}
            var Q101;
            {var subQ0=sQuery(id+"F0.wireOp",EDGE,"E17.left");var subQ1=sQuery(id+"F0.wireOp",EDGE,"E7.bottom");var subQ2=makeQuery(id+"F0.imprint","INTERSECT",VERTEX,{"derivedFrom":[subQ1,subQ0]});Q101=makeQuery(id+"F0.imprint","IMPRINT",FACE,{"disambiguationData":[TD([[makeQuery(id+"F0.imprint","IMPRINT",EDGE,{"disambiguationData":[TD([[subQ2,-1.0]])],"derivedFrom":subQ1}),1.0]])]});}
            var Q102;
            {var subQ0=sQuery(id+"F0.wireOp",EDGE,"E18.left");var subQ1=sQuery(id+"F0.wireOp",EDGE,"E7.bottom");var subQ2=makeQuery(id+"F0.imprint","INTERSECT",VERTEX,{"derivedFrom":[subQ1,subQ0]});Q102=makeQuery(id+"F0.imprint","IMPRINT",FACE,{"disambiguationData":[TD([[makeQuery(id+"F0.imprint","IMPRINT",EDGE,{"disambiguationData":[TD([[subQ2,-1.0]])],"derivedFrom":subQ1}),1.0]])]});}
            var Q103;
            {var subQ0=sQuery(id+"F0.wireOp",EDGE,"E17.left");var subQ1=sQuery(id+"F0.wireOp",EDGE,"E6.bottom");var subQ2=makeQuery(id+"F0.imprint","INTERSECT",VERTEX,{"derivedFrom":[subQ1,subQ0]});Q103=makeQuery(id+"F0.imprint","IMPRINT",FACE,{"disambiguationData":[TD([[makeQuery(id+"F0.imprint","IMPRINT",EDGE,{"disambiguationData":[TD([[subQ2,-1.0]])],"derivedFrom":subQ1}),1.0]])]});}
            var Q104;
            {var subQ0=sQuery(id+"F0.wireOp",EDGE,"E18.left");var subQ1=sQuery(id+"F0.wireOp",EDGE,"E6.bottom");var subQ2=makeQuery(id+"F0.imprint","INTERSECT",VERTEX,{"derivedFrom":[subQ1,subQ0]});Q104=makeQuery(id+"F0.imprint","IMPRINT",FACE,{"disambiguationData":[TD([[makeQuery(id+"F0.imprint","IMPRINT",EDGE,{"disambiguationData":[TD([[subQ2,-1.0]])],"derivedFrom":subQ1}),1.0]])]});}
            var Q105;
            {var subQ0=sQuery(id+"F0.wireOp",EDGE,"E17.left");var subQ1=sQuery(id+"F0.wireOp",EDGE,"E5.bottom");var subQ2=makeQuery(id+"F0.imprint","INTERSECT",VERTEX,{"derivedFrom":[subQ1,subQ0]});Q105=makeQuery(id+"F0.imprint","IMPRINT",FACE,{"disambiguationData":[TD([[makeQuery(id+"F0.imprint","IMPRINT",EDGE,{"disambiguationData":[TD([[subQ2,-1.0]])],"derivedFrom":subQ1}),1.0]])]});}
            var Q106;
            {var subQ0=sQuery(id+"F0.wireOp",EDGE,"E18.left");var subQ1=sQuery(id+"F0.wireOp",EDGE,"E5.bottom");var subQ2=makeQuery(id+"F0.imprint","INTERSECT",VERTEX,{"derivedFrom":[subQ1,subQ0]});Q106=makeQuery(id+"F0.imprint","IMPRINT",FACE,{"disambiguationData":[TD([[makeQuery(id+"F0.imprint","IMPRINT",EDGE,{"disambiguationData":[TD([[subQ2,-1.0]])],"derivedFrom":subQ1}),1.0]])]});}
            var Q107;
            {var subQ0=sQuery(id+"F0.wireOp",EDGE,"E16.left");var subQ1=sQuery(id+"F0.wireOp",EDGE,"E5.bottom");var subQ2=makeQuery(id+"F0.imprint","INTERSECT",VERTEX,{"derivedFrom":[subQ1,subQ0]});Q107=makeQuery(id+"F0.imprint","IMPRINT",FACE,{"disambiguationData":[TD([[makeQuery(id+"F0.imprint","IMPRINT",EDGE,{"disambiguationData":[TD([[subQ2,-1.0]])],"derivedFrom":subQ1}),1.0]])]});}
            var Q108;
            {var subQ0=sQuery(id+"F0.wireOp",EDGE,"E16.left");var subQ1=sQuery(id+"F0.wireOp",EDGE,"E6.bottom");var subQ2=makeQuery(id+"F0.imprint","INTERSECT",VERTEX,{"derivedFrom":[subQ1,subQ0]});Q108=makeQuery(id+"F0.imprint","IMPRINT",FACE,{"disambiguationData":[TD([[makeQuery(id+"F0.imprint","IMPRINT",EDGE,{"disambiguationData":[TD([[subQ2,-1.0]])],"derivedFrom":subQ1}),1.0]])]});}
            var Q109;
            {var subQ0=sQuery(id+"F0.wireOp",EDGE,"E15.left");var subQ1=sQuery(id+"F0.wireOp",EDGE,"E5.bottom");var subQ2=makeQuery(id+"F0.imprint","INTERSECT",VERTEX,{"derivedFrom":[subQ1,subQ0]});Q109=makeQuery(id+"F0.imprint","IMPRINT",FACE,{"disambiguationData":[TD([[makeQuery(id+"F0.imprint","IMPRINT",EDGE,{"disambiguationData":[TD([[subQ2,-1.0]])],"derivedFrom":subQ1}),1.0]])]});}
            var Q110;
            {var subQ0=sQuery(id+"F0.wireOp",EDGE,"E15.left");var subQ1=sQuery(id+"F0.wireOp",EDGE,"E6.bottom");var subQ2=makeQuery(id+"F0.imprint","INTERSECT",VERTEX,{"derivedFrom":[subQ1,subQ0]});Q110=makeQuery(id+"F0.imprint","IMPRINT",FACE,{"disambiguationData":[TD([[makeQuery(id+"F0.imprint","IMPRINT",EDGE,{"disambiguationData":[TD([[subQ2,-1.0]])],"derivedFrom":subQ1}),1.0]])]});}
            var Q111;
            {var subQ0=sQuery(id+"F0.wireOp",EDGE,"E14.left");var subQ1=sQuery(id+"F0.wireOp",EDGE,"E6.bottom");var subQ2=makeQuery(id+"F0.imprint","INTERSECT",VERTEX,{"derivedFrom":[subQ1,subQ0]});Q111=makeQuery(id+"F0.imprint","IMPRINT",FACE,{"disambiguationData":[TD([[makeQuery(id+"F0.imprint","IMPRINT",EDGE,{"disambiguationData":[TD([[subQ2,-1.0]])],"derivedFrom":subQ1}),1.0]])]});}
            var Q112;
            {var subQ0=sQuery(id+"F0.wireOp",EDGE,"E14.left");var subQ1=sQuery(id+"F0.wireOp",EDGE,"E5.bottom");var subQ2=makeQuery(id+"F0.imprint","INTERSECT",VERTEX,{"derivedFrom":[subQ1,subQ0]});Q112=makeQuery(id+"F0.imprint","IMPRINT",FACE,{"disambiguationData":[TD([[makeQuery(id+"F0.imprint","IMPRINT",EDGE,{"disambiguationData":[TD([[subQ2,-1.0]])],"derivedFrom":subQ1}),1.0]])]});}
            var Q113;
            {var subQ0=sQuery(id+"F0.wireOp",EDGE,"E13.left");var subQ1=sQuery(id+"F0.wireOp",EDGE,"E5.bottom");var subQ2=makeQuery(id+"F0.imprint","INTERSECT",VERTEX,{"derivedFrom":[subQ1,subQ0]});Q113=makeQuery(id+"F0.imprint","IMPRINT",FACE,{"disambiguationData":[TD([[makeQuery(id+"F0.imprint","IMPRINT",EDGE,{"disambiguationData":[TD([[subQ2,-1.0]])],"derivedFrom":subQ1}),1.0]])]});}
            var Q114;
            {var subQ0=sQuery(id+"F0.wireOp",EDGE,"E12.left");var subQ1=sQuery(id+"F0.wireOp",EDGE,"E5.bottom");var subQ2=makeQuery(id+"F0.imprint","INTERSECT",VERTEX,{"derivedFrom":[subQ1,subQ0]});Q114=makeQuery(id+"F0.imprint","IMPRINT",FACE,{"disambiguationData":[TD([[makeQuery(id+"F0.imprint","IMPRINT",EDGE,{"disambiguationData":[TD([[subQ2,-1.0]])],"derivedFrom":subQ1}),1.0]])]});}
            var Q115;
            {var subQ0=sQuery(id+"F0.wireOp",EDGE,"E11.left");var subQ1=sQuery(id+"F0.wireOp",EDGE,"E5.bottom");var subQ2=makeQuery(id+"F0.imprint","INTERSECT",VERTEX,{"derivedFrom":[subQ1,subQ0]});Q115=makeQuery(id+"F0.imprint","IMPRINT",FACE,{"disambiguationData":[TD([[makeQuery(id+"F0.imprint","IMPRINT",EDGE,{"disambiguationData":[TD([[subQ2,-1.0]])],"derivedFrom":subQ1}),1.0]])]});}
            var Q116;
            {var subQ0=sQuery(id+"F0.wireOp",EDGE,"E11.left");var subQ1=sQuery(id+"F0.wireOp",EDGE,"E6.bottom");var subQ2=makeQuery(id+"F0.imprint","INTERSECT",VERTEX,{"derivedFrom":[subQ1,subQ0]});Q116=makeQuery(id+"F0.imprint","IMPRINT",FACE,{"disambiguationData":[TD([[makeQuery(id+"F0.imprint","IMPRINT",EDGE,{"disambiguationData":[TD([[subQ2,-1.0]])],"derivedFrom":subQ1}),1.0]])]});}
            var Q117;
            {var subQ0=sQuery(id+"F0.wireOp",EDGE,"E12.left");var subQ1=sQuery(id+"F0.wireOp",EDGE,"E6.bottom");var subQ2=makeQuery(id+"F0.imprint","INTERSECT",VERTEX,{"derivedFrom":[subQ1,subQ0]});Q117=makeQuery(id+"F0.imprint","IMPRINT",FACE,{"disambiguationData":[TD([[makeQuery(id+"F0.imprint","IMPRINT",EDGE,{"disambiguationData":[TD([[subQ2,-1.0]])],"derivedFrom":subQ1}),1.0]])]});}
            var Q118;
            {var subQ0=sQuery(id+"F0.wireOp",EDGE,"E13.left");var subQ1=sQuery(id+"F0.wireOp",EDGE,"E6.bottom");var subQ2=makeQuery(id+"F0.imprint","INTERSECT",VERTEX,{"derivedFrom":[subQ1,subQ0]});Q118=makeQuery(id+"F0.imprint","IMPRINT",FACE,{"disambiguationData":[TD([[makeQuery(id+"F0.imprint","IMPRINT",EDGE,{"disambiguationData":[TD([[subQ2,-1.0]])],"derivedFrom":subQ1}),1.0]])]});}
            var Q119;
            {var subQ0=sQuery(id+"F0.wireOp",EDGE,"E11.left");var subQ1=sQuery(id+"F0.wireOp",EDGE,"E7.bottom");var subQ2=makeQuery(id+"F0.imprint","INTERSECT",VERTEX,{"derivedFrom":[subQ1,subQ0]});Q119=makeQuery(id+"F0.imprint","IMPRINT",FACE,{"disambiguationData":[TD([[makeQuery(id+"F0.imprint","IMPRINT",EDGE,{"disambiguationData":[TD([[subQ2,-1.0]])],"derivedFrom":subQ1}),1.0]])]});}
            var Q120;
            {var subQ0=sQuery(id+"F0.wireOp",EDGE,"E12.left");var subQ1=sQuery(id+"F0.wireOp",EDGE,"E7.bottom");var subQ2=makeQuery(id+"F0.imprint","INTERSECT",VERTEX,{"derivedFrom":[subQ1,subQ0]});Q120=makeQuery(id+"F0.imprint","IMPRINT",FACE,{"disambiguationData":[TD([[makeQuery(id+"F0.imprint","IMPRINT",EDGE,{"disambiguationData":[TD([[subQ2,-1.0]])],"derivedFrom":subQ1}),1.0]])]});}
            var Q121;
            {var subQ0=sQuery(id+"F0.wireOp",EDGE,"E13.left");var subQ1=sQuery(id+"F0.wireOp",EDGE,"E7.bottom");var subQ2=makeQuery(id+"F0.imprint","INTERSECT",VERTEX,{"derivedFrom":[subQ1,subQ0]});Q121=makeQuery(id+"F0.imprint","IMPRINT",FACE,{"disambiguationData":[TD([[makeQuery(id+"F0.imprint","IMPRINT",EDGE,{"disambiguationData":[TD([[subQ2,-1.0]])],"derivedFrom":subQ1}),1.0]])]});}
            var Q122;
            {var subQ0=sQuery(id+"F0.wireOp",EDGE,"E14.left");var subQ1=sQuery(id+"F0.wireOp",EDGE,"E7.bottom");var subQ2=makeQuery(id+"F0.imprint","INTERSECT",VERTEX,{"derivedFrom":[subQ1,subQ0]});Q122=makeQuery(id+"F0.imprint","IMPRINT",FACE,{"disambiguationData":[TD([[makeQuery(id+"F0.imprint","IMPRINT",EDGE,{"disambiguationData":[TD([[subQ2,-1.0]])],"derivedFrom":subQ1}),1.0]])]});}
            var Q123;
            {var subQ0=sQuery(id+"F0.wireOp",EDGE,"E15.left");var subQ1=sQuery(id+"F0.wireOp",EDGE,"E7.bottom");var subQ2=makeQuery(id+"F0.imprint","INTERSECT",VERTEX,{"derivedFrom":[subQ1,subQ0]});Q123=makeQuery(id+"F0.imprint","IMPRINT",FACE,{"disambiguationData":[TD([[makeQuery(id+"F0.imprint","IMPRINT",EDGE,{"disambiguationData":[TD([[subQ2,-1.0]])],"derivedFrom":subQ1}),1.0]])]});}
            var Q124;
            {var subQ0=sQuery(id+"F0.wireOp",EDGE,"E16.left");var subQ1=sQuery(id+"F0.wireOp",EDGE,"E7.bottom");var subQ2=makeQuery(id+"F0.imprint","INTERSECT",VERTEX,{"derivedFrom":[subQ1,subQ0]});Q124=makeQuery(id+"F0.imprint","IMPRINT",FACE,{"disambiguationData":[TD([[makeQuery(id+"F0.imprint","IMPRINT",EDGE,{"disambiguationData":[TD([[subQ2,-1.0]])],"derivedFrom":subQ1}),1.0]])]});}
            extrude(context, id + "F4", {"entities" : qUnion([Q0, Q1, Q2, Q3, Q4, Q5, Q6, Q7, Q8, Q9, Q10, Q11, Q12, Q13, Q14, Q15, Q16, Q17, Q18, Q19, Q20, Q21, Q22, Q23, Q24, Q25, Q26, Q27, Q28, Q29, Q30, Q31, Q32, Q33, Q34, Q35, Q36, Q37, Q38, Q39, Q40, Q41, Q42, Q43, Q44, Q45, Q46, Q47, Q48, Q49, Q50, Q51, Q52, Q53, Q54, Q55, Q56, Q57, Q58, Q59, Q60, Q61, Q62, Q63, Q64, Q65, Q66, Q67, Q68, Q69, Q70, Q71, Q72, Q73, Q74, Q75, Q76, Q77, Q78, Q79, Q80, Q81, Q82, Q83, Q84, Q85, Q86, Q87, Q88, Q89, Q90, Q91, Q92, Q93, Q94, Q95, Q96, Q97, Q98, Q99, Q100, Q101, Q102, Q103, Q104, Q105, Q106, Q107, Q108, Q109, Q110, Q111, Q112, Q113, Q114, Q115, Q116, Q117, Q118, Q119, Q120, Q121, Q122, Q123, Q124]), "depth" : 101.6 * mm, "offsetDistance" : 25.4 * mm});
        }
    });
